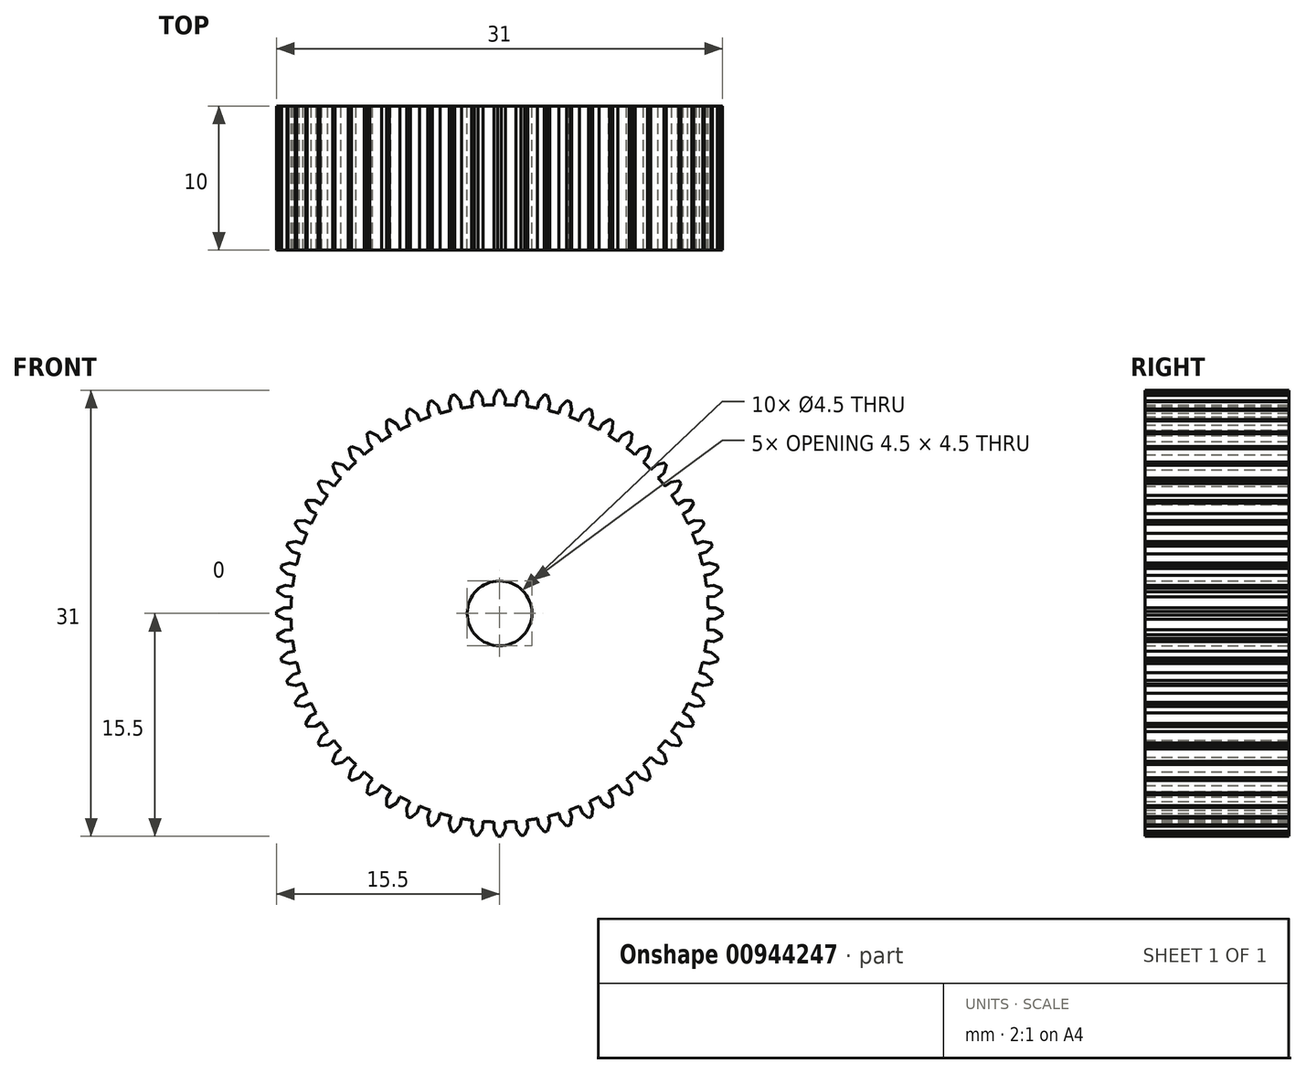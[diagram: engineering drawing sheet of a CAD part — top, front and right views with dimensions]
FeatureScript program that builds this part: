
annotation { "Feature Type Name" : "Feature", "Feature Type Description" : "" }
export const myFeature = defineFeature(function(context is Context, id is Id, definition is map)
    precondition{}
    {
        {
            var Q0;
            Q0=qCreatedBy(makeId("Front.planeOp"),FACE);
            var sketch = newSketch(context, id + "F0", { "sketchPlane" : qUnion([Q0])});
            skCircle(sketch, "E0", {"center": v(0, 0) * mm, "radius": 14.5 * mm});
            skCircle(sketch, "E1", {"center": v(0, 0) * mm, "radius": 15 * mm, "construction": true});
            skCircle(sketch, "E2", {"center": v(0, 0) * mm, "radius": 15.5 * mm, "construction": true});
            skLineSegment(sketch, "E3", {"start": v(0, 0) * mm, "end": v(0, 25.34) * mm, "construction": true});
            skLineSegment(sketch, "E4", {"start": v(0, 25.34) * mm, "end": v(0, 0) * mm, "construction": true});
            skLineSegment(sketch, "E5", {"start": v(-0.38, 14.5) * mm, "end": v(-0.4, 15) * mm});
            skLineSegment(sketch, "E6", {"start": v(0.38, 14.5) * mm, "end": v(0.4, 15) * mm});
            skLineSegment(sketch, "E7", {"start": v(-0.39, 15) * mm, "end": v(-0.12, 15.5) * mm});
            skLineSegment(sketch, "E8", {"start": v(0.39, 15) * mm, "end": v(0.12, 15.5) * mm});
            skArc(sketch, "E9", {"start": v(-0.12, 15.5) * mm, "mid": v(0, 15.5) * mm, "end": v(0.12, 15.5) * mm});
            skPoint(sketch, "E10.newPointB", {"position": v(-0.57, 21.86) * mm});
            skArc(sketch, "E10.filletArc", {"start": v(-0.39, 15) * mm, "mid": v(-0.4, 15) * mm, "end": v(-0.4, 14.98) * mm});
            skPoint(sketch, "E11.newPointA", {"position": v(0.57, 21.86) * mm});
            skArc(sketch, "E11.filletArc", {"start": v(0.4, 14.98) * mm, "mid": v(0.4, 15) * mm, "end": v(0.39, 15) * mm});
            skLineSegment(sketch, "E12.1.0", {"start": v(-1.14, 14.46) * mm, "end": v(-1.18, 14.95) * mm});
            skLineSegment(sketch, "E12.1.1", {"start": v(-1.9, 14.38) * mm, "end": v(-1.96, 14.87) * mm});
            skArc(sketch, "E12.1.2", {"start": v(-1.95, 14.88) * mm, "mid": v(-1.96, 14.87) * mm, "end": v(-1.96, 14.86) * mm});
            skLineSegment(sketch, "E12.1.3", {"start": v(-1.95, 14.88) * mm, "end": v(-1.74, 15.4) * mm});
            skArc(sketch, "E12.1.4", {"start": v(-1.18, 14.94) * mm, "mid": v(-1.18, 14.95) * mm, "end": v(-1.18, 14.96) * mm});
            skLineSegment(sketch, "E12.1.5", {"start": v(-1.18, 14.96) * mm, "end": v(-1.5, 15.43) * mm});
            skArc(sketch, "E12.1.6", {"start": v(-1.74, 15.4) * mm, "mid": v(-1.62, 15.42) * mm, "end": v(-1.5, 15.43) * mm});
            skLineSegment(sketch, "E12.2.0", {"start": v(-2.64, 14.26) * mm, "end": v(-2.73, 14.75) * mm});
            skLineSegment(sketch, "E12.2.1", {"start": v(-3.38, 14.1) * mm, "end": v(-3.5, 14.59) * mm});
            skArc(sketch, "E12.2.2", {"start": v(-3.5, 14.6) * mm, "mid": v(-3.5, 14.59) * mm, "end": v(-3.5, 14.57) * mm});
            skLineSegment(sketch, "E12.2.3", {"start": v(-3.5, 14.6) * mm, "end": v(-3.34, 15.14) * mm});
            skArc(sketch, "E12.2.4", {"start": v(-2.73, 14.74) * mm, "mid": v(-2.74, 14.75) * mm, "end": v(-2.74, 14.76) * mm});
            skLineSegment(sketch, "E12.2.5", {"start": v(-2.74, 14.76) * mm, "end": v(-3.1, 15.19) * mm});
            skArc(sketch, "E12.2.6", {"start": v(-3.34, 15.14) * mm, "mid": v(-3.22, 15.16) * mm, "end": v(-3.1, 15.19) * mm});
            skLineSegment(sketch, "E12.3.0", {"start": v(-4.12, 13.9) * mm, "end": v(-4.26, 14.38) * mm});
            skLineSegment(sketch, "E12.3.1", {"start": v(-4.84, 13.67) * mm, "end": v(-5, 14.14) * mm});
            skArc(sketch, "E12.3.2", {"start": v(-5, 14.15) * mm, "mid": v(-5, 14.14) * mm, "end": v(-5, 14.13) * mm});
            skLineSegment(sketch, "E12.3.3", {"start": v(-5, 14.15) * mm, "end": v(-4.9, 14.7) * mm});
            skArc(sketch, "E12.3.4", {"start": v(-4.26, 14.37) * mm, "mid": v(-4.26, 14.38) * mm, "end": v(-4.27, 14.4) * mm});
            skLineSegment(sketch, "E12.3.5", {"start": v(-4.27, 14.4) * mm, "end": v(-4.68, 14.78) * mm});
            skArc(sketch, "E12.3.6", {"start": v(-4.9, 14.7) * mm, "mid": v(-4.79, 14.74) * mm, "end": v(-4.68, 14.78) * mm});
            skLineSegment(sketch, "E12.4.0", {"start": v(-5.55, 13.4) * mm, "end": v(-5.74, 13.86) * mm});
            skLineSegment(sketch, "E12.4.1", {"start": v(-6.24, 13.09) * mm, "end": v(-6.46, 13.54) * mm});
            skArc(sketch, "E12.4.2", {"start": v(-6.46, 13.55) * mm, "mid": v(-6.46, 13.54) * mm, "end": v(-6.45, 13.53) * mm});
            skLineSegment(sketch, "E12.4.3", {"start": v(-6.46, 13.55) * mm, "end": v(-6.41, 14.11) * mm});
            skArc(sketch, "E12.4.4", {"start": v(-5.74, 13.85) * mm, "mid": v(-5.74, 13.86) * mm, "end": v(-5.75, 13.87) * mm});
            skLineSegment(sketch, "E12.4.5", {"start": v(-5.75, 13.87) * mm, "end": v(-6.2, 14.2) * mm});
            skArc(sketch, "E12.4.6", {"start": v(-6.41, 14.11) * mm, "mid": v(-6.3, 14.16) * mm, "end": v(-6.2, 14.2) * mm});
            skLineSegment(sketch, "E12.5.0", {"start": v(-6.92, 12.74) * mm, "end": v(-7.16, 13.18) * mm});
            skLineSegment(sketch, "E12.5.1", {"start": v(-7.58, 12.36) * mm, "end": v(-7.84, 12.79) * mm});
            skArc(sketch, "E12.5.2", {"start": v(-7.84, 12.8) * mm, "mid": v(-7.84, 12.8) * mm, "end": v(-7.83, 12.78) * mm});
            skLineSegment(sketch, "E12.5.3", {"start": v(-7.84, 12.8) * mm, "end": v(-7.85, 13.36) * mm});
            skArc(sketch, "E12.5.4", {"start": v(-7.15, 13.17) * mm, "mid": v(-7.16, 13.18) * mm, "end": v(-7.17, 13.19) * mm});
            skLineSegment(sketch, "E12.5.5", {"start": v(-7.17, 13.19) * mm, "end": v(-7.65, 13.48) * mm});
            skArc(sketch, "E12.5.6", {"start": v(-7.85, 13.36) * mm, "mid": v(-7.75, 13.42) * mm, "end": v(-7.65, 13.48) * mm});
            skLineSegment(sketch, "E12.6.0", {"start": v(-8.21, 11.95) * mm, "end": v(-8.5, 12.36) * mm});
            skLineSegment(sketch, "E12.6.1", {"start": v(-8.83, 11.5) * mm, "end": v(-9.13, 11.9) * mm});
            skArc(sketch, "E12.6.2", {"start": v(-9.13, 11.91) * mm, "mid": v(-9.13, 11.9) * mm, "end": v(-9.12, 11.89) * mm});
            skLineSegment(sketch, "E12.6.3", {"start": v(-9.13, 11.91) * mm, "end": v(-9.2, 12.47) * mm});
            skArc(sketch, "E12.6.4", {"start": v(-8.49, 12.35) * mm, "mid": v(-8.5, 12.36) * mm, "end": v(-8.5, 12.37) * mm});
            skLineSegment(sketch, "E12.6.5", {"start": v(-8.5, 12.37) * mm, "end": v(-9.01, 12.6) * mm});
            skArc(sketch, "E12.6.6", {"start": v(-9.2, 12.47) * mm, "mid": v(-9.11, 12.54) * mm, "end": v(-9.01, 12.6) * mm});
            skLineSegment(sketch, "E12.7.0", {"start": v(-9.42, 11.03) * mm, "end": v(-9.74, 11.4) * mm});
            skLineSegment(sketch, "E12.7.1", {"start": v(-9.98, 10.52) * mm, "end": v(-10.33, 10.88) * mm});
            skArc(sketch, "E12.7.2", {"start": v(-10.33, 10.9) * mm, "mid": v(-10.32, 10.88) * mm, "end": v(-10.32, 10.87) * mm});
            skLineSegment(sketch, "E12.7.3", {"start": v(-10.33, 10.9) * mm, "end": v(-10.46, 11.44) * mm});
            skArc(sketch, "E12.7.4", {"start": v(-9.73, 11.4) * mm, "mid": v(-9.74, 11.4) * mm, "end": v(-9.75, 11.41) * mm});
            skLineSegment(sketch, "E12.7.5", {"start": v(-9.75, 11.41) * mm, "end": v(-10.28, 11.6) * mm});
            skArc(sketch, "E12.7.6", {"start": v(-10.46, 11.44) * mm, "mid": v(-10.37, 11.52) * mm, "end": v(-10.28, 11.6) * mm});
            skLineSegment(sketch, "E12.8.0", {"start": v(-10.52, 9.98) * mm, "end": v(-10.88, 10.33) * mm});
            skLineSegment(sketch, "E12.8.1", {"start": v(-11.03, 9.42) * mm, "end": v(-11.4, 9.74) * mm});
            skArc(sketch, "E12.8.2", {"start": v(-11.41, 9.75) * mm, "mid": v(-11.4, 9.74) * mm, "end": v(-11.4, 9.73) * mm});
            skLineSegment(sketch, "E12.8.3", {"start": v(-11.41, 9.75) * mm, "end": v(-11.6, 10.28) * mm});
            skArc(sketch, "E12.8.4", {"start": v(-10.87, 10.32) * mm, "mid": v(-10.88, 10.32) * mm, "end": v(-10.9, 10.33) * mm});
            skLineSegment(sketch, "E12.8.5", {"start": v(-10.9, 10.33) * mm, "end": v(-11.44, 10.46) * mm});
            skArc(sketch, "E12.8.6", {"start": v(-11.6, 10.28) * mm, "mid": v(-11.52, 10.37) * mm, "end": v(-11.44, 10.46) * mm});
            skLineSegment(sketch, "E12.9.0", {"start": v(-11.5, 8.83) * mm, "end": v(-11.9, 9.13) * mm});
            skLineSegment(sketch, "E12.9.1", {"start": v(-11.95, 8.21) * mm, "end": v(-12.36, 8.5) * mm});
            skArc(sketch, "E12.9.2", {"start": v(-12.37, 8.5) * mm, "mid": v(-12.36, 8.5) * mm, "end": v(-12.35, 8.49) * mm});
            skLineSegment(sketch, "E12.9.3", {"start": v(-12.37, 8.5) * mm, "end": v(-12.6, 9.01) * mm});
            skArc(sketch, "E12.9.4", {"start": v(-11.89, 9.12) * mm, "mid": v(-11.9, 9.13) * mm, "end": v(-11.91, 9.13) * mm});
            skLineSegment(sketch, "E12.9.5", {"start": v(-11.91, 9.13) * mm, "end": v(-12.47, 9.2) * mm});
            skArc(sketch, "E12.9.6", {"start": v(-12.6, 9.01) * mm, "mid": v(-12.54, 9.11) * mm, "end": v(-12.47, 9.2) * mm});
            skLineSegment(sketch, "E12.10.0", {"start": v(-12.36, 7.58) * mm, "end": v(-12.79, 7.84) * mm});
            skLineSegment(sketch, "E12.10.1", {"start": v(-12.74, 6.92) * mm, "end": v(-13.18, 7.16) * mm});
            skArc(sketch, "E12.10.2", {"start": v(-13.19, 7.17) * mm, "mid": v(-13.18, 7.16) * mm, "end": v(-13.17, 7.15) * mm});
            skLineSegment(sketch, "E12.10.3", {"start": v(-13.19, 7.17) * mm, "end": v(-13.48, 7.65) * mm});
            skArc(sketch, "E12.10.4", {"start": v(-12.78, 7.83) * mm, "mid": v(-12.8, 7.84) * mm, "end": v(-12.8, 7.84) * mm});
            skLineSegment(sketch, "E12.10.5", {"start": v(-12.8, 7.84) * mm, "end": v(-13.36, 7.85) * mm});
            skArc(sketch, "E12.10.6", {"start": v(-13.48, 7.65) * mm, "mid": v(-13.42, 7.75) * mm, "end": v(-13.36, 7.85) * mm});
            skLineSegment(sketch, "E12.11.0", {"start": v(-13.09, 6.24) * mm, "end": v(-13.54, 6.46) * mm});
            skLineSegment(sketch, "E12.11.1", {"start": v(-13.4, 5.55) * mm, "end": v(-13.86, 5.74) * mm});
            skArc(sketch, "E12.11.2", {"start": v(-13.87, 5.75) * mm, "mid": v(-13.86, 5.74) * mm, "end": v(-13.85, 5.74) * mm});
            skLineSegment(sketch, "E12.11.3", {"start": v(-13.87, 5.75) * mm, "end": v(-14.2, 6.2) * mm});
            skArc(sketch, "E12.11.4", {"start": v(-13.53, 6.45) * mm, "mid": v(-13.54, 6.46) * mm, "end": v(-13.55, 6.46) * mm});
            skLineSegment(sketch, "E12.11.5", {"start": v(-13.55, 6.46) * mm, "end": v(-14.11, 6.41) * mm});
            skArc(sketch, "E12.11.6", {"start": v(-14.2, 6.2) * mm, "mid": v(-14.16, 6.3) * mm, "end": v(-14.11, 6.41) * mm});
            skLineSegment(sketch, "E12.12.0", {"start": v(-13.67, 4.84) * mm, "end": v(-14.14, 5) * mm});
            skLineSegment(sketch, "E12.12.1", {"start": v(-13.9, 4.12) * mm, "end": v(-14.38, 4.26) * mm});
            skArc(sketch, "E12.12.2", {"start": v(-14.4, 4.27) * mm, "mid": v(-14.38, 4.26) * mm, "end": v(-14.37, 4.26) * mm});
            skLineSegment(sketch, "E12.12.3", {"start": v(-14.4, 4.27) * mm, "end": v(-14.78, 4.68) * mm});
            skArc(sketch, "E12.12.4", {"start": v(-14.13, 5) * mm, "mid": v(-14.14, 5) * mm, "end": v(-14.15, 5) * mm});
            skLineSegment(sketch, "E12.12.5", {"start": v(-14.15, 5) * mm, "end": v(-14.7, 4.9) * mm});
            skArc(sketch, "E12.12.6", {"start": v(-14.78, 4.68) * mm, "mid": v(-14.74, 4.79) * mm, "end": v(-14.7, 4.9) * mm});
            skLineSegment(sketch, "E12.13.0", {"start": v(-14.1, 3.38) * mm, "end": v(-14.59, 3.5) * mm});
            skLineSegment(sketch, "E12.13.1", {"start": v(-14.26, 2.64) * mm, "end": v(-14.75, 2.73) * mm});
            skArc(sketch, "E12.13.2", {"start": v(-14.76, 2.74) * mm, "mid": v(-14.75, 2.74) * mm, "end": v(-14.74, 2.73) * mm});
            skLineSegment(sketch, "E12.13.3", {"start": v(-14.76, 2.74) * mm, "end": v(-15.19, 3.1) * mm});
            skArc(sketch, "E12.13.4", {"start": v(-14.57, 3.5) * mm, "mid": v(-14.59, 3.5) * mm, "end": v(-14.6, 3.5) * mm});
            skLineSegment(sketch, "E12.13.5", {"start": v(-14.6, 3.5) * mm, "end": v(-15.14, 3.34) * mm});
            skArc(sketch, "E12.13.6", {"start": v(-15.19, 3.1) * mm, "mid": v(-15.16, 3.22) * mm, "end": v(-15.14, 3.34) * mm});
            skLineSegment(sketch, "E12.14.0", {"start": v(-14.38, 1.9) * mm, "end": v(-14.87, 1.96) * mm});
            skLineSegment(sketch, "E12.14.1", {"start": v(-14.46, 1.14) * mm, "end": v(-14.95, 1.18) * mm});
            skArc(sketch, "E12.14.2", {"start": v(-14.96, 1.18) * mm, "mid": v(-14.95, 1.18) * mm, "end": v(-14.94, 1.18) * mm});
            skLineSegment(sketch, "E12.14.3", {"start": v(-14.96, 1.18) * mm, "end": v(-15.43, 1.5) * mm});
            skArc(sketch, "E12.14.4", {"start": v(-14.86, 1.96) * mm, "mid": v(-14.87, 1.96) * mm, "end": v(-14.88, 1.95) * mm});
            skLineSegment(sketch, "E12.14.5", {"start": v(-14.88, 1.95) * mm, "end": v(-15.4, 1.74) * mm});
            skArc(sketch, "E12.14.6", {"start": v(-15.43, 1.5) * mm, "mid": v(-15.42, 1.62) * mm, "end": v(-15.4, 1.74) * mm});
            skLineSegment(sketch, "E12.15.0", {"start": v(-14.5, 0.38) * mm, "end": v(-15, 0.4) * mm});
            skLineSegment(sketch, "E12.15.1", {"start": v(-14.5, -0.38) * mm, "end": v(-15, -0.4) * mm});
            skArc(sketch, "E12.15.2", {"start": v(-15, -0.39) * mm, "mid": v(-15, -0.4) * mm, "end": v(-14.98, -0.4) * mm});
            skLineSegment(sketch, "E12.15.3", {"start": v(-15, -0.39) * mm, "end": v(-15.5, -0.12) * mm});
            skArc(sketch, "E12.15.4", {"start": v(-14.98, 0.4) * mm, "mid": v(-15, 0.4) * mm, "end": v(-15, 0.39) * mm});
            skLineSegment(sketch, "E12.15.5", {"start": v(-15, 0.39) * mm, "end": v(-15.5, 0.12) * mm});
            skArc(sketch, "E12.15.6", {"start": v(-15.5, -0.12) * mm, "mid": v(-15.5, 0) * mm, "end": v(-15.5, 0.12) * mm});
            skLineSegment(sketch, "E12.16.0", {"start": v(-14.46, -1.14) * mm, "end": v(-14.95, -1.18) * mm});
            skLineSegment(sketch, "E12.16.1", {"start": v(-14.38, -1.9) * mm, "end": v(-14.87, -1.96) * mm});
            skArc(sketch, "E12.16.2", {"start": v(-14.88, -1.95) * mm, "mid": v(-14.87, -1.96) * mm, "end": v(-14.86, -1.96) * mm});
            skLineSegment(sketch, "E12.16.3", {"start": v(-14.88, -1.95) * mm, "end": v(-15.4, -1.74) * mm});
            skArc(sketch, "E12.16.4", {"start": v(-14.94, -1.18) * mm, "mid": v(-14.95, -1.18) * mm, "end": v(-14.96, -1.18) * mm});
            skLineSegment(sketch, "E12.16.5", {"start": v(-14.96, -1.18) * mm, "end": v(-15.43, -1.5) * mm});
            skArc(sketch, "E12.16.6", {"start": v(-15.4, -1.74) * mm, "mid": v(-15.42, -1.62) * mm, "end": v(-15.43, -1.5) * mm});
            skLineSegment(sketch, "E12.17.0", {"start": v(-14.26, -2.64) * mm, "end": v(-14.75, -2.73) * mm});
            skLineSegment(sketch, "E12.17.1", {"start": v(-14.1, -3.38) * mm, "end": v(-14.59, -3.5) * mm});
            skArc(sketch, "E12.17.2", {"start": v(-14.6, -3.5) * mm, "mid": v(-14.59, -3.5) * mm, "end": v(-14.57, -3.5) * mm});
            skLineSegment(sketch, "E12.17.3", {"start": v(-14.6, -3.5) * mm, "end": v(-15.14, -3.34) * mm});
            skArc(sketch, "E12.17.4", {"start": v(-14.74, -2.73) * mm, "mid": v(-14.75, -2.74) * mm, "end": v(-14.76, -2.74) * mm});
            skLineSegment(sketch, "E12.17.5", {"start": v(-14.76, -2.74) * mm, "end": v(-15.19, -3.1) * mm});
            skArc(sketch, "E12.17.6", {"start": v(-15.14, -3.34) * mm, "mid": v(-15.16, -3.22) * mm, "end": v(-15.19, -3.1) * mm});
            skLineSegment(sketch, "E12.18.0", {"start": v(-13.9, -4.12) * mm, "end": v(-14.38, -4.26) * mm});
            skLineSegment(sketch, "E12.18.1", {"start": v(-13.67, -4.84) * mm, "end": v(-14.14, -5) * mm});
            skArc(sketch, "E12.18.2", {"start": v(-14.15, -5) * mm, "mid": v(-14.14, -5) * mm, "end": v(-14.13, -5) * mm});
            skLineSegment(sketch, "E12.18.3", {"start": v(-14.15, -5) * mm, "end": v(-14.7, -4.9) * mm});
            skArc(sketch, "E12.18.4", {"start": v(-14.37, -4.26) * mm, "mid": v(-14.38, -4.26) * mm, "end": v(-14.4, -4.27) * mm});
            skLineSegment(sketch, "E12.18.5", {"start": v(-14.4, -4.27) * mm, "end": v(-14.78, -4.68) * mm});
            skArc(sketch, "E12.18.6", {"start": v(-14.7, -4.9) * mm, "mid": v(-14.74, -4.79) * mm, "end": v(-14.78, -4.68) * mm});
            skLineSegment(sketch, "E12.19.0", {"start": v(-13.4, -5.55) * mm, "end": v(-13.86, -5.74) * mm});
            skLineSegment(sketch, "E12.19.1", {"start": v(-13.09, -6.24) * mm, "end": v(-13.54, -6.46) * mm});
            skArc(sketch, "E12.19.2", {"start": v(-13.55, -6.46) * mm, "mid": v(-13.54, -6.46) * mm, "end": v(-13.53, -6.45) * mm});
            skLineSegment(sketch, "E12.19.3", {"start": v(-13.55, -6.46) * mm, "end": v(-14.11, -6.41) * mm});
            skArc(sketch, "E12.19.4", {"start": v(-13.85, -5.74) * mm, "mid": v(-13.86, -5.74) * mm, "end": v(-13.87, -5.75) * mm});
            skLineSegment(sketch, "E12.19.5", {"start": v(-13.87, -5.75) * mm, "end": v(-14.2, -6.2) * mm});
            skArc(sketch, "E12.19.6", {"start": v(-14.11, -6.41) * mm, "mid": v(-14.16, -6.3) * mm, "end": v(-14.2, -6.2) * mm});
            skLineSegment(sketch, "E12.20.0", {"start": v(-12.74, -6.92) * mm, "end": v(-13.18, -7.16) * mm});
            skLineSegment(sketch, "E12.20.1", {"start": v(-12.36, -7.58) * mm, "end": v(-12.79, -7.84) * mm});
            skArc(sketch, "E12.20.2", {"start": v(-12.8, -7.84) * mm, "mid": v(-12.8, -7.84) * mm, "end": v(-12.78, -7.83) * mm});
            skLineSegment(sketch, "E12.20.3", {"start": v(-12.8, -7.84) * mm, "end": v(-13.36, -7.85) * mm});
            skArc(sketch, "E12.20.4", {"start": v(-13.17, -7.15) * mm, "mid": v(-13.18, -7.16) * mm, "end": v(-13.19, -7.17) * mm});
            skLineSegment(sketch, "E12.20.5", {"start": v(-13.19, -7.17) * mm, "end": v(-13.48, -7.65) * mm});
            skArc(sketch, "E12.20.6", {"start": v(-13.36, -7.85) * mm, "mid": v(-13.42, -7.75) * mm, "end": v(-13.48, -7.65) * mm});
            skLineSegment(sketch, "E12.21.0", {"start": v(-11.95, -8.21) * mm, "end": v(-12.36, -8.5) * mm});
            skLineSegment(sketch, "E12.21.1", {"start": v(-11.5, -8.83) * mm, "end": v(-11.9, -9.13) * mm});
            skArc(sketch, "E12.21.2", {"start": v(-11.91, -9.13) * mm, "mid": v(-11.9, -9.13) * mm, "end": v(-11.89, -9.12) * mm});
            skLineSegment(sketch, "E12.21.3", {"start": v(-11.91, -9.13) * mm, "end": v(-12.47, -9.2) * mm});
            skArc(sketch, "E12.21.4", {"start": v(-12.35, -8.49) * mm, "mid": v(-12.36, -8.5) * mm, "end": v(-12.37, -8.5) * mm});
            skLineSegment(sketch, "E12.21.5", {"start": v(-12.37, -8.5) * mm, "end": v(-12.6, -9.01) * mm});
            skArc(sketch, "E12.21.6", {"start": v(-12.47, -9.2) * mm, "mid": v(-12.54, -9.11) * mm, "end": v(-12.6, -9.01) * mm});
            skLineSegment(sketch, "E12.22.0", {"start": v(-11.03, -9.42) * mm, "end": v(-11.4, -9.74) * mm});
            skLineSegment(sketch, "E12.22.1", {"start": v(-10.52, -9.98) * mm, "end": v(-10.88, -10.33) * mm});
            skArc(sketch, "E12.22.2", {"start": v(-10.9, -10.33) * mm, "mid": v(-10.88, -10.32) * mm, "end": v(-10.87, -10.32) * mm});
            skLineSegment(sketch, "E12.22.3", {"start": v(-10.9, -10.33) * mm, "end": v(-11.44, -10.46) * mm});
            skArc(sketch, "E12.22.4", {"start": v(-11.4, -9.73) * mm, "mid": v(-11.4, -9.74) * mm, "end": v(-11.41, -9.75) * mm});
            skLineSegment(sketch, "E12.22.5", {"start": v(-11.41, -9.75) * mm, "end": v(-11.6, -10.28) * mm});
            skArc(sketch, "E12.22.6", {"start": v(-11.44, -10.46) * mm, "mid": v(-11.52, -10.37) * mm, "end": v(-11.6, -10.28) * mm});
            skLineSegment(sketch, "E12.23.0", {"start": v(-9.98, -10.52) * mm, "end": v(-10.33, -10.88) * mm});
            skLineSegment(sketch, "E12.23.1", {"start": v(-9.42, -11.03) * mm, "end": v(-9.74, -11.4) * mm});
            skArc(sketch, "E12.23.2", {"start": v(-9.75, -11.41) * mm, "mid": v(-9.74, -11.4) * mm, "end": v(-9.73, -11.4) * mm});
            skLineSegment(sketch, "E12.23.3", {"start": v(-9.75, -11.41) * mm, "end": v(-10.28, -11.6) * mm});
            skArc(sketch, "E12.23.4", {"start": v(-10.32, -10.87) * mm, "mid": v(-10.32, -10.88) * mm, "end": v(-10.33, -10.9) * mm});
            skLineSegment(sketch, "E12.23.5", {"start": v(-10.33, -10.9) * mm, "end": v(-10.46, -11.44) * mm});
            skArc(sketch, "E12.23.6", {"start": v(-10.28, -11.6) * mm, "mid": v(-10.37, -11.52) * mm, "end": v(-10.46, -11.44) * mm});
            skLineSegment(sketch, "E12.24.0", {"start": v(-8.83, -11.5) * mm, "end": v(-9.13, -11.9) * mm});
            skLineSegment(sketch, "E12.24.1", {"start": v(-8.21, -11.95) * mm, "end": v(-8.5, -12.36) * mm});
            skArc(sketch, "E12.24.2", {"start": v(-8.5, -12.37) * mm, "mid": v(-8.5, -12.36) * mm, "end": v(-8.49, -12.35) * mm});
            skLineSegment(sketch, "E12.24.3", {"start": v(-8.5, -12.37) * mm, "end": v(-9.01, -12.6) * mm});
            skArc(sketch, "E12.24.4", {"start": v(-9.12, -11.89) * mm, "mid": v(-9.13, -11.9) * mm, "end": v(-9.13, -11.91) * mm});
            skLineSegment(sketch, "E12.24.5", {"start": v(-9.13, -11.91) * mm, "end": v(-9.2, -12.47) * mm});
            skArc(sketch, "E12.24.6", {"start": v(-9.01, -12.6) * mm, "mid": v(-9.11, -12.54) * mm, "end": v(-9.2, -12.47) * mm});
            skLineSegment(sketch, "E12.25.0", {"start": v(-7.58, -12.36) * mm, "end": v(-7.84, -12.79) * mm});
            skLineSegment(sketch, "E12.25.1", {"start": v(-6.92, -12.74) * mm, "end": v(-7.16, -13.18) * mm});
            skArc(sketch, "E12.25.2", {"start": v(-7.17, -13.19) * mm, "mid": v(-7.16, -13.18) * mm, "end": v(-7.15, -13.17) * mm});
            skLineSegment(sketch, "E12.25.3", {"start": v(-7.17, -13.19) * mm, "end": v(-7.65, -13.48) * mm});
            skArc(sketch, "E12.25.4", {"start": v(-7.83, -12.78) * mm, "mid": v(-7.84, -12.8) * mm, "end": v(-7.84, -12.8) * mm});
            skLineSegment(sketch, "E12.25.5", {"start": v(-7.84, -12.8) * mm, "end": v(-7.85, -13.36) * mm});
            skArc(sketch, "E12.25.6", {"start": v(-7.65, -13.48) * mm, "mid": v(-7.75, -13.42) * mm, "end": v(-7.85, -13.36) * mm});
            skLineSegment(sketch, "E12.26.0", {"start": v(-6.24, -13.09) * mm, "end": v(-6.46, -13.54) * mm});
            skLineSegment(sketch, "E12.26.1", {"start": v(-5.55, -13.4) * mm, "end": v(-5.74, -13.86) * mm});
            skArc(sketch, "E12.26.2", {"start": v(-5.75, -13.87) * mm, "mid": v(-5.74, -13.86) * mm, "end": v(-5.74, -13.85) * mm});
            skLineSegment(sketch, "E12.26.3", {"start": v(-5.75, -13.87) * mm, "end": v(-6.2, -14.2) * mm});
            skArc(sketch, "E12.26.4", {"start": v(-6.45, -13.53) * mm, "mid": v(-6.46, -13.54) * mm, "end": v(-6.46, -13.55) * mm});
            skLineSegment(sketch, "E12.26.5", {"start": v(-6.46, -13.55) * mm, "end": v(-6.41, -14.11) * mm});
            skArc(sketch, "E12.26.6", {"start": v(-6.2, -14.2) * mm, "mid": v(-6.3, -14.16) * mm, "end": v(-6.41, -14.11) * mm});
            skLineSegment(sketch, "E12.27.0", {"start": v(-4.84, -13.67) * mm, "end": v(-5, -14.14) * mm});
            skLineSegment(sketch, "E12.27.1", {"start": v(-4.12, -13.9) * mm, "end": v(-4.26, -14.38) * mm});
            skArc(sketch, "E12.27.2", {"start": v(-4.27, -14.4) * mm, "mid": v(-4.26, -14.38) * mm, "end": v(-4.26, -14.37) * mm});
            skLineSegment(sketch, "E12.27.3", {"start": v(-4.27, -14.4) * mm, "end": v(-4.68, -14.78) * mm});
            skArc(sketch, "E12.27.4", {"start": v(-5, -14.13) * mm, "mid": v(-5, -14.14) * mm, "end": v(-5, -14.15) * mm});
            skLineSegment(sketch, "E12.27.5", {"start": v(-5, -14.15) * mm, "end": v(-4.9, -14.7) * mm});
            skArc(sketch, "E12.27.6", {"start": v(-4.68, -14.78) * mm, "mid": v(-4.79, -14.74) * mm, "end": v(-4.9, -14.7) * mm});
            skLineSegment(sketch, "E12.28.0", {"start": v(-3.38, -14.1) * mm, "end": v(-3.5, -14.59) * mm});
            skLineSegment(sketch, "E12.28.1", {"start": v(-2.64, -14.26) * mm, "end": v(-2.73, -14.75) * mm});
            skArc(sketch, "E12.28.2", {"start": v(-2.74, -14.76) * mm, "mid": v(-2.74, -14.75) * mm, "end": v(-2.73, -14.74) * mm});
            skLineSegment(sketch, "E12.28.3", {"start": v(-2.74, -14.76) * mm, "end": v(-3.1, -15.19) * mm});
            skArc(sketch, "E12.28.4", {"start": v(-3.5, -14.57) * mm, "mid": v(-3.5, -14.59) * mm, "end": v(-3.5, -14.6) * mm});
            skLineSegment(sketch, "E12.28.5", {"start": v(-3.5, -14.6) * mm, "end": v(-3.34, -15.14) * mm});
            skArc(sketch, "E12.28.6", {"start": v(-3.1, -15.19) * mm, "mid": v(-3.22, -15.16) * mm, "end": v(-3.34, -15.14) * mm});
            skLineSegment(sketch, "E12.29.0", {"start": v(-1.9, -14.38) * mm, "end": v(-1.96, -14.87) * mm});
            skLineSegment(sketch, "E12.29.1", {"start": v(-1.14, -14.46) * mm, "end": v(-1.18, -14.95) * mm});
            skArc(sketch, "E12.29.2", {"start": v(-1.18, -14.96) * mm, "mid": v(-1.18, -14.95) * mm, "end": v(-1.18, -14.94) * mm});
            skLineSegment(sketch, "E12.29.3", {"start": v(-1.18, -14.96) * mm, "end": v(-1.5, -15.43) * mm});
            skArc(sketch, "E12.29.4", {"start": v(-1.96, -14.86) * mm, "mid": v(-1.96, -14.87) * mm, "end": v(-1.95, -14.88) * mm});
            skLineSegment(sketch, "E12.29.5", {"start": v(-1.95, -14.88) * mm, "end": v(-1.74, -15.4) * mm});
            skArc(sketch, "E12.29.6", {"start": v(-1.5, -15.43) * mm, "mid": v(-1.62, -15.42) * mm, "end": v(-1.74, -15.4) * mm});
            skLineSegment(sketch, "E12.30.0", {"start": v(-0.38, -14.5) * mm, "end": v(-0.4, -15) * mm});
            skLineSegment(sketch, "E12.30.1", {"start": v(0.38, -14.5) * mm, "end": v(0.4, -15) * mm});
            skArc(sketch, "E12.30.2", {"start": v(0.39, -15) * mm, "mid": v(0.4, -15) * mm, "end": v(0.4, -14.98) * mm});
            skLineSegment(sketch, "E12.30.3", {"start": v(0.39, -15) * mm, "end": v(0.12, -15.5) * mm});
            skArc(sketch, "E12.30.4", {"start": v(-0.4, -14.98) * mm, "mid": v(-0.4, -15) * mm, "end": v(-0.39, -15) * mm});
            skLineSegment(sketch, "E12.30.5", {"start": v(-0.39, -15) * mm, "end": v(-0.12, -15.5) * mm});
            skArc(sketch, "E12.30.6", {"start": v(0.12, -15.5) * mm, "mid": v(0, -15.5) * mm, "end": v(-0.12, -15.5) * mm});
            skLineSegment(sketch, "E12.31.0", {"start": v(1.14, -14.46) * mm, "end": v(1.18, -14.95) * mm});
            skLineSegment(sketch, "E12.31.1", {"start": v(1.9, -14.38) * mm, "end": v(1.96, -14.87) * mm});
            skArc(sketch, "E12.31.2", {"start": v(1.95, -14.88) * mm, "mid": v(1.96, -14.87) * mm, "end": v(1.96, -14.86) * mm});
            skLineSegment(sketch, "E12.31.3", {"start": v(1.95, -14.88) * mm, "end": v(1.74, -15.4) * mm});
            skArc(sketch, "E12.31.4", {"start": v(1.18, -14.94) * mm, "mid": v(1.18, -14.95) * mm, "end": v(1.18, -14.96) * mm});
            skLineSegment(sketch, "E12.31.5", {"start": v(1.18, -14.96) * mm, "end": v(1.5, -15.43) * mm});
            skArc(sketch, "E12.31.6", {"start": v(1.74, -15.4) * mm, "mid": v(1.62, -15.42) * mm, "end": v(1.5, -15.43) * mm});
            skLineSegment(sketch, "E12.32.0", {"start": v(2.64, -14.26) * mm, "end": v(2.73, -14.75) * mm});
            skLineSegment(sketch, "E12.32.1", {"start": v(3.38, -14.1) * mm, "end": v(3.5, -14.59) * mm});
            skArc(sketch, "E12.32.2", {"start": v(3.5, -14.6) * mm, "mid": v(3.5, -14.59) * mm, "end": v(3.5, -14.57) * mm});
            skLineSegment(sketch, "E12.32.3", {"start": v(3.5, -14.6) * mm, "end": v(3.34, -15.14) * mm});
            skArc(sketch, "E12.32.4", {"start": v(2.73, -14.74) * mm, "mid": v(2.74, -14.75) * mm, "end": v(2.74, -14.76) * mm});
            skLineSegment(sketch, "E12.32.5", {"start": v(2.74, -14.76) * mm, "end": v(3.1, -15.19) * mm});
            skArc(sketch, "E12.32.6", {"start": v(3.34, -15.14) * mm, "mid": v(3.22, -15.16) * mm, "end": v(3.1, -15.19) * mm});
            skLineSegment(sketch, "E12.33.0", {"start": v(4.12, -13.9) * mm, "end": v(4.26, -14.38) * mm});
            skLineSegment(sketch, "E12.33.1", {"start": v(4.84, -13.67) * mm, "end": v(5, -14.14) * mm});
            skArc(sketch, "E12.33.2", {"start": v(5, -14.15) * mm, "mid": v(5, -14.14) * mm, "end": v(5, -14.13) * mm});
            skLineSegment(sketch, "E12.33.3", {"start": v(5, -14.15) * mm, "end": v(4.9, -14.7) * mm});
            skArc(sketch, "E12.33.4", {"start": v(4.26, -14.37) * mm, "mid": v(4.26, -14.38) * mm, "end": v(4.27, -14.4) * mm});
            skLineSegment(sketch, "E12.33.5", {"start": v(4.27, -14.4) * mm, "end": v(4.68, -14.78) * mm});
            skArc(sketch, "E12.33.6", {"start": v(4.9, -14.7) * mm, "mid": v(4.79, -14.74) * mm, "end": v(4.68, -14.78) * mm});
            skLineSegment(sketch, "E12.34.0", {"start": v(5.55, -13.4) * mm, "end": v(5.74, -13.86) * mm});
            skLineSegment(sketch, "E12.34.1", {"start": v(6.24, -13.09) * mm, "end": v(6.46, -13.54) * mm});
            skArc(sketch, "E12.34.2", {"start": v(6.46, -13.55) * mm, "mid": v(6.46, -13.54) * mm, "end": v(6.45, -13.53) * mm});
            skLineSegment(sketch, "E12.34.3", {"start": v(6.46, -13.55) * mm, "end": v(6.41, -14.11) * mm});
            skArc(sketch, "E12.34.4", {"start": v(5.74, -13.85) * mm, "mid": v(5.74, -13.86) * mm, "end": v(5.75, -13.87) * mm});
            skLineSegment(sketch, "E12.34.5", {"start": v(5.75, -13.87) * mm, "end": v(6.2, -14.2) * mm});
            skArc(sketch, "E12.34.6", {"start": v(6.41, -14.11) * mm, "mid": v(6.3, -14.16) * mm, "end": v(6.2, -14.2) * mm});
            skLineSegment(sketch, "E12.35.0", {"start": v(6.92, -12.74) * mm, "end": v(7.16, -13.18) * mm});
            skLineSegment(sketch, "E12.35.1", {"start": v(7.58, -12.36) * mm, "end": v(7.84, -12.79) * mm});
            skArc(sketch, "E12.35.2", {"start": v(7.84, -12.8) * mm, "mid": v(7.84, -12.8) * mm, "end": v(7.83, -12.78) * mm});
            skLineSegment(sketch, "E12.35.3", {"start": v(7.84, -12.8) * mm, "end": v(7.85, -13.36) * mm});
            skArc(sketch, "E12.35.4", {"start": v(7.15, -13.17) * mm, "mid": v(7.16, -13.18) * mm, "end": v(7.17, -13.19) * mm});
            skLineSegment(sketch, "E12.35.5", {"start": v(7.17, -13.19) * mm, "end": v(7.65, -13.48) * mm});
            skArc(sketch, "E12.35.6", {"start": v(7.85, -13.36) * mm, "mid": v(7.75, -13.42) * mm, "end": v(7.65, -13.48) * mm});
            skLineSegment(sketch, "E12.36.0", {"start": v(8.21, -11.95) * mm, "end": v(8.5, -12.36) * mm});
            skLineSegment(sketch, "E12.36.1", {"start": v(8.83, -11.5) * mm, "end": v(9.13, -11.9) * mm});
            skArc(sketch, "E12.36.2", {"start": v(9.13, -11.91) * mm, "mid": v(9.13, -11.9) * mm, "end": v(9.12, -11.89) * mm});
            skLineSegment(sketch, "E12.36.3", {"start": v(9.13, -11.91) * mm, "end": v(9.2, -12.47) * mm});
            skArc(sketch, "E12.36.4", {"start": v(8.49, -12.35) * mm, "mid": v(8.5, -12.36) * mm, "end": v(8.5, -12.37) * mm});
            skLineSegment(sketch, "E12.36.5", {"start": v(8.5, -12.37) * mm, "end": v(9.01, -12.6) * mm});
            skArc(sketch, "E12.36.6", {"start": v(9.2, -12.47) * mm, "mid": v(9.11, -12.54) * mm, "end": v(9.01, -12.6) * mm});
            skLineSegment(sketch, "E12.37.0", {"start": v(9.42, -11.03) * mm, "end": v(9.74, -11.4) * mm});
            skLineSegment(sketch, "E12.37.1", {"start": v(9.98, -10.52) * mm, "end": v(10.33, -10.88) * mm});
            skArc(sketch, "E12.37.2", {"start": v(10.33, -10.9) * mm, "mid": v(10.32, -10.88) * mm, "end": v(10.32, -10.87) * mm});
            skLineSegment(sketch, "E12.37.3", {"start": v(10.33, -10.9) * mm, "end": v(10.46, -11.44) * mm});
            skArc(sketch, "E12.37.4", {"start": v(9.73, -11.4) * mm, "mid": v(9.74, -11.4) * mm, "end": v(9.75, -11.41) * mm});
            skLineSegment(sketch, "E12.37.5", {"start": v(9.75, -11.41) * mm, "end": v(10.28, -11.6) * mm});
            skArc(sketch, "E12.37.6", {"start": v(10.46, -11.44) * mm, "mid": v(10.37, -11.52) * mm, "end": v(10.28, -11.6) * mm});
            skLineSegment(sketch, "E12.38.0", {"start": v(10.52, -9.98) * mm, "end": v(10.88, -10.33) * mm});
            skLineSegment(sketch, "E12.38.1", {"start": v(11.03, -9.42) * mm, "end": v(11.4, -9.74) * mm});
            skArc(sketch, "E12.38.2", {"start": v(11.41, -9.75) * mm, "mid": v(11.4, -9.74) * mm, "end": v(11.4, -9.73) * mm});
            skLineSegment(sketch, "E12.38.3", {"start": v(11.41, -9.75) * mm, "end": v(11.6, -10.28) * mm});
            skArc(sketch, "E12.38.4", {"start": v(10.87, -10.32) * mm, "mid": v(10.88, -10.32) * mm, "end": v(10.9, -10.33) * mm});
            skLineSegment(sketch, "E12.38.5", {"start": v(10.9, -10.33) * mm, "end": v(11.44, -10.46) * mm});
            skArc(sketch, "E12.38.6", {"start": v(11.6, -10.28) * mm, "mid": v(11.52, -10.37) * mm, "end": v(11.44, -10.46) * mm});
            skLineSegment(sketch, "E12.39.0", {"start": v(11.5, -8.83) * mm, "end": v(11.9, -9.13) * mm});
            skLineSegment(sketch, "E12.39.1", {"start": v(11.95, -8.21) * mm, "end": v(12.36, -8.5) * mm});
            skArc(sketch, "E12.39.2", {"start": v(12.37, -8.5) * mm, "mid": v(12.36, -8.5) * mm, "end": v(12.35, -8.49) * mm});
            skLineSegment(sketch, "E12.39.3", {"start": v(12.37, -8.5) * mm, "end": v(12.6, -9.01) * mm});
            skArc(sketch, "E12.39.4", {"start": v(11.89, -9.12) * mm, "mid": v(11.9, -9.13) * mm, "end": v(11.91, -9.13) * mm});
            skLineSegment(sketch, "E12.39.5", {"start": v(11.91, -9.13) * mm, "end": v(12.47, -9.2) * mm});
            skArc(sketch, "E12.39.6", {"start": v(12.6, -9.01) * mm, "mid": v(12.54, -9.11) * mm, "end": v(12.47, -9.2) * mm});
            skLineSegment(sketch, "E12.40.0", {"start": v(12.36, -7.58) * mm, "end": v(12.79, -7.84) * mm});
            skLineSegment(sketch, "E12.40.1", {"start": v(12.74, -6.92) * mm, "end": v(13.18, -7.16) * mm});
            skArc(sketch, "E12.40.2", {"start": v(13.19, -7.17) * mm, "mid": v(13.18, -7.16) * mm, "end": v(13.17, -7.15) * mm});
            skLineSegment(sketch, "E12.40.3", {"start": v(13.19, -7.17) * mm, "end": v(13.48, -7.65) * mm});
            skArc(sketch, "E12.40.4", {"start": v(12.78, -7.83) * mm, "mid": v(12.8, -7.84) * mm, "end": v(12.8, -7.84) * mm});
            skLineSegment(sketch, "E12.40.5", {"start": v(12.8, -7.84) * mm, "end": v(13.36, -7.85) * mm});
            skArc(sketch, "E12.40.6", {"start": v(13.48, -7.65) * mm, "mid": v(13.42, -7.75) * mm, "end": v(13.36, -7.85) * mm});
            skLineSegment(sketch, "E12.41.0", {"start": v(13.09, -6.24) * mm, "end": v(13.54, -6.46) * mm});
            skLineSegment(sketch, "E12.41.1", {"start": v(13.4, -5.55) * mm, "end": v(13.86, -5.74) * mm});
            skArc(sketch, "E12.41.2", {"start": v(13.87, -5.75) * mm, "mid": v(13.86, -5.74) * mm, "end": v(13.85, -5.74) * mm});
            skLineSegment(sketch, "E12.41.3", {"start": v(13.87, -5.75) * mm, "end": v(14.2, -6.2) * mm});
            skArc(sketch, "E12.41.4", {"start": v(13.53, -6.45) * mm, "mid": v(13.54, -6.46) * mm, "end": v(13.55, -6.46) * mm});
            skLineSegment(sketch, "E12.41.5", {"start": v(13.55, -6.46) * mm, "end": v(14.11, -6.41) * mm});
            skArc(sketch, "E12.41.6", {"start": v(14.2, -6.2) * mm, "mid": v(14.16, -6.3) * mm, "end": v(14.11, -6.41) * mm});
            skLineSegment(sketch, "E12.42.0", {"start": v(13.67, -4.84) * mm, "end": v(14.14, -5) * mm});
            skLineSegment(sketch, "E12.42.1", {"start": v(13.9, -4.12) * mm, "end": v(14.38, -4.26) * mm});
            skArc(sketch, "E12.42.2", {"start": v(14.4, -4.27) * mm, "mid": v(14.38, -4.26) * mm, "end": v(14.37, -4.26) * mm});
            skLineSegment(sketch, "E12.42.3", {"start": v(14.4, -4.27) * mm, "end": v(14.78, -4.68) * mm});
            skArc(sketch, "E12.42.4", {"start": v(14.13, -5) * mm, "mid": v(14.14, -5) * mm, "end": v(14.15, -5) * mm});
            skLineSegment(sketch, "E12.42.5", {"start": v(14.15, -5) * mm, "end": v(14.7, -4.9) * mm});
            skArc(sketch, "E12.42.6", {"start": v(14.78, -4.68) * mm, "mid": v(14.74, -4.79) * mm, "end": v(14.7, -4.9) * mm});
            skLineSegment(sketch, "E12.43.0", {"start": v(14.1, -3.38) * mm, "end": v(14.59, -3.5) * mm});
            skLineSegment(sketch, "E12.43.1", {"start": v(14.26, -2.64) * mm, "end": v(14.75, -2.73) * mm});
            skArc(sketch, "E12.43.2", {"start": v(14.76, -2.74) * mm, "mid": v(14.75, -2.74) * mm, "end": v(14.74, -2.73) * mm});
            skLineSegment(sketch, "E12.43.3", {"start": v(14.76, -2.74) * mm, "end": v(15.19, -3.1) * mm});
            skArc(sketch, "E12.43.4", {"start": v(14.57, -3.5) * mm, "mid": v(14.59, -3.5) * mm, "end": v(14.6, -3.5) * mm});
            skLineSegment(sketch, "E12.43.5", {"start": v(14.6, -3.5) * mm, "end": v(15.14, -3.34) * mm});
            skArc(sketch, "E12.43.6", {"start": v(15.19, -3.1) * mm, "mid": v(15.16, -3.22) * mm, "end": v(15.14, -3.34) * mm});
            skLineSegment(sketch, "E12.44.0", {"start": v(14.38, -1.9) * mm, "end": v(14.87, -1.96) * mm});
            skLineSegment(sketch, "E12.44.1", {"start": v(14.46, -1.14) * mm, "end": v(14.95, -1.18) * mm});
            skArc(sketch, "E12.44.2", {"start": v(14.96, -1.18) * mm, "mid": v(14.95, -1.18) * mm, "end": v(14.94, -1.18) * mm});
            skLineSegment(sketch, "E12.44.3", {"start": v(14.96, -1.18) * mm, "end": v(15.43, -1.5) * mm});
            skArc(sketch, "E12.44.4", {"start": v(14.86, -1.96) * mm, "mid": v(14.87, -1.96) * mm, "end": v(14.88, -1.95) * mm});
            skLineSegment(sketch, "E12.44.5", {"start": v(14.88, -1.95) * mm, "end": v(15.4, -1.74) * mm});
            skArc(sketch, "E12.44.6", {"start": v(15.43, -1.5) * mm, "mid": v(15.42, -1.62) * mm, "end": v(15.4, -1.74) * mm});
            skLineSegment(sketch, "E12.45.0", {"start": v(14.5, -0.38) * mm, "end": v(15, -0.4) * mm});
            skLineSegment(sketch, "E12.45.1", {"start": v(14.5, 0.38) * mm, "end": v(15, 0.4) * mm});
            skArc(sketch, "E12.45.2", {"start": v(15, 0.39) * mm, "mid": v(15, 0.4) * mm, "end": v(14.98, 0.4) * mm});
            skLineSegment(sketch, "E12.45.3", {"start": v(15, 0.39) * mm, "end": v(15.5, 0.12) * mm});
            skArc(sketch, "E12.45.4", {"start": v(14.98, -0.4) * mm, "mid": v(15, -0.4) * mm, "end": v(15, -0.39) * mm});
            skLineSegment(sketch, "E12.45.5", {"start": v(15, -0.39) * mm, "end": v(15.5, -0.12) * mm});
            skArc(sketch, "E12.45.6", {"start": v(15.5, 0.12) * mm, "mid": v(15.5, 0) * mm, "end": v(15.5, -0.12) * mm});
            skLineSegment(sketch, "E12.46.0", {"start": v(14.46, 1.14) * mm, "end": v(14.95, 1.18) * mm});
            skLineSegment(sketch, "E12.46.1", {"start": v(14.38, 1.9) * mm, "end": v(14.87, 1.96) * mm});
            skArc(sketch, "E12.46.2", {"start": v(14.88, 1.95) * mm, "mid": v(14.87, 1.96) * mm, "end": v(14.86, 1.96) * mm});
            skLineSegment(sketch, "E12.46.3", {"start": v(14.88, 1.95) * mm, "end": v(15.4, 1.74) * mm});
            skArc(sketch, "E12.46.4", {"start": v(14.94, 1.18) * mm, "mid": v(14.95, 1.18) * mm, "end": v(14.96, 1.18) * mm});
            skLineSegment(sketch, "E12.46.5", {"start": v(14.96, 1.18) * mm, "end": v(15.43, 1.5) * mm});
            skArc(sketch, "E12.46.6", {"start": v(15.4, 1.74) * mm, "mid": v(15.42, 1.62) * mm, "end": v(15.43, 1.5) * mm});
            skLineSegment(sketch, "E12.47.0", {"start": v(14.26, 2.64) * mm, "end": v(14.75, 2.73) * mm});
            skLineSegment(sketch, "E12.47.1", {"start": v(14.1, 3.38) * mm, "end": v(14.59, 3.5) * mm});
            skArc(sketch, "E12.47.2", {"start": v(14.6, 3.5) * mm, "mid": v(14.59, 3.5) * mm, "end": v(14.57, 3.5) * mm});
            skLineSegment(sketch, "E12.47.3", {"start": v(14.6, 3.5) * mm, "end": v(15.14, 3.34) * mm});
            skArc(sketch, "E12.47.4", {"start": v(14.74, 2.73) * mm, "mid": v(14.75, 2.74) * mm, "end": v(14.76, 2.74) * mm});
            skLineSegment(sketch, "E12.47.5", {"start": v(14.76, 2.74) * mm, "end": v(15.19, 3.1) * mm});
            skArc(sketch, "E12.47.6", {"start": v(15.14, 3.34) * mm, "mid": v(15.16, 3.22) * mm, "end": v(15.19, 3.1) * mm});
            skLineSegment(sketch, "E12.48.0", {"start": v(13.9, 4.12) * mm, "end": v(14.38, 4.26) * mm});
            skLineSegment(sketch, "E12.48.1", {"start": v(13.67, 4.84) * mm, "end": v(14.14, 5) * mm});
            skArc(sketch, "E12.48.2", {"start": v(14.15, 5) * mm, "mid": v(14.14, 5) * mm, "end": v(14.13, 5) * mm});
            skLineSegment(sketch, "E12.48.3", {"start": v(14.15, 5) * mm, "end": v(14.7, 4.9) * mm});
            skArc(sketch, "E12.48.4", {"start": v(14.37, 4.26) * mm, "mid": v(14.38, 4.26) * mm, "end": v(14.4, 4.27) * mm});
            skLineSegment(sketch, "E12.48.5", {"start": v(14.4, 4.27) * mm, "end": v(14.78, 4.68) * mm});
            skArc(sketch, "E12.48.6", {"start": v(14.7, 4.9) * mm, "mid": v(14.74, 4.79) * mm, "end": v(14.78, 4.68) * mm});
            skLineSegment(sketch, "E12.49.0", {"start": v(13.4, 5.55) * mm, "end": v(13.86, 5.74) * mm});
            skLineSegment(sketch, "E12.49.1", {"start": v(13.09, 6.24) * mm, "end": v(13.54, 6.46) * mm});
            skArc(sketch, "E12.49.2", {"start": v(13.55, 6.46) * mm, "mid": v(13.54, 6.46) * mm, "end": v(13.53, 6.45) * mm});
            skLineSegment(sketch, "E12.49.3", {"start": v(13.55, 6.46) * mm, "end": v(14.11, 6.41) * mm});
            skArc(sketch, "E12.49.4", {"start": v(13.85, 5.74) * mm, "mid": v(13.86, 5.74) * mm, "end": v(13.87, 5.75) * mm});
            skLineSegment(sketch, "E12.49.5", {"start": v(13.87, 5.75) * mm, "end": v(14.2, 6.2) * mm});
            skArc(sketch, "E12.49.6", {"start": v(14.11, 6.41) * mm, "mid": v(14.16, 6.3) * mm, "end": v(14.2, 6.2) * mm});
            skLineSegment(sketch, "E12.50.0", {"start": v(12.74, 6.92) * mm, "end": v(13.18, 7.16) * mm});
            skLineSegment(sketch, "E12.50.1", {"start": v(12.36, 7.58) * mm, "end": v(12.79, 7.84) * mm});
            skArc(sketch, "E12.50.2", {"start": v(12.8, 7.84) * mm, "mid": v(12.8, 7.84) * mm, "end": v(12.78, 7.83) * mm});
            skLineSegment(sketch, "E12.50.3", {"start": v(12.8, 7.84) * mm, "end": v(13.36, 7.85) * mm});
            skArc(sketch, "E12.50.4", {"start": v(13.17, 7.15) * mm, "mid": v(13.18, 7.16) * mm, "end": v(13.19, 7.17) * mm});
            skLineSegment(sketch, "E12.50.5", {"start": v(13.19, 7.17) * mm, "end": v(13.48, 7.65) * mm});
            skArc(sketch, "E12.50.6", {"start": v(13.36, 7.85) * mm, "mid": v(13.42, 7.75) * mm, "end": v(13.48, 7.65) * mm});
            skLineSegment(sketch, "E12.51.0", {"start": v(11.95, 8.21) * mm, "end": v(12.36, 8.5) * mm});
            skLineSegment(sketch, "E12.51.1", {"start": v(11.5, 8.83) * mm, "end": v(11.9, 9.13) * mm});
            skArc(sketch, "E12.51.2", {"start": v(11.91, 9.13) * mm, "mid": v(11.9, 9.13) * mm, "end": v(11.89, 9.12) * mm});
            skLineSegment(sketch, "E12.51.3", {"start": v(11.91, 9.13) * mm, "end": v(12.47, 9.2) * mm});
            skArc(sketch, "E12.51.4", {"start": v(12.35, 8.49) * mm, "mid": v(12.36, 8.5) * mm, "end": v(12.37, 8.5) * mm});
            skLineSegment(sketch, "E12.51.5", {"start": v(12.37, 8.5) * mm, "end": v(12.6, 9.01) * mm});
            skArc(sketch, "E12.51.6", {"start": v(12.47, 9.2) * mm, "mid": v(12.54, 9.11) * mm, "end": v(12.6, 9.01) * mm});
            skLineSegment(sketch, "E12.52.0", {"start": v(11.03, 9.42) * mm, "end": v(11.4, 9.74) * mm});
            skLineSegment(sketch, "E12.52.1", {"start": v(10.52, 9.98) * mm, "end": v(10.88, 10.33) * mm});
            skArc(sketch, "E12.52.2", {"start": v(10.9, 10.33) * mm, "mid": v(10.88, 10.32) * mm, "end": v(10.87, 10.32) * mm});
            skLineSegment(sketch, "E12.52.3", {"start": v(10.9, 10.33) * mm, "end": v(11.44, 10.46) * mm});
            skArc(sketch, "E12.52.4", {"start": v(11.4, 9.73) * mm, "mid": v(11.4, 9.74) * mm, "end": v(11.41, 9.75) * mm});
            skLineSegment(sketch, "E12.52.5", {"start": v(11.41, 9.75) * mm, "end": v(11.6, 10.28) * mm});
            skArc(sketch, "E12.52.6", {"start": v(11.44, 10.46) * mm, "mid": v(11.52, 10.37) * mm, "end": v(11.6, 10.28) * mm});
            skLineSegment(sketch, "E12.53.0", {"start": v(9.98, 10.52) * mm, "end": v(10.33, 10.88) * mm});
            skLineSegment(sketch, "E12.53.1", {"start": v(9.42, 11.03) * mm, "end": v(9.74, 11.4) * mm});
            skArc(sketch, "E12.53.2", {"start": v(9.75, 11.41) * mm, "mid": v(9.74, 11.4) * mm, "end": v(9.73, 11.4) * mm});
            skLineSegment(sketch, "E12.53.3", {"start": v(9.75, 11.41) * mm, "end": v(10.28, 11.6) * mm});
            skArc(sketch, "E12.53.4", {"start": v(10.32, 10.87) * mm, "mid": v(10.32, 10.88) * mm, "end": v(10.33, 10.9) * mm});
            skLineSegment(sketch, "E12.53.5", {"start": v(10.33, 10.9) * mm, "end": v(10.46, 11.44) * mm});
            skArc(sketch, "E12.53.6", {"start": v(10.28, 11.6) * mm, "mid": v(10.37, 11.52) * mm, "end": v(10.46, 11.44) * mm});
            skLineSegment(sketch, "E12.54.0", {"start": v(8.83, 11.5) * mm, "end": v(9.13, 11.9) * mm});
            skLineSegment(sketch, "E12.54.1", {"start": v(8.21, 11.95) * mm, "end": v(8.5, 12.36) * mm});
            skArc(sketch, "E12.54.2", {"start": v(8.5, 12.37) * mm, "mid": v(8.5, 12.36) * mm, "end": v(8.49, 12.35) * mm});
            skLineSegment(sketch, "E12.54.3", {"start": v(8.5, 12.37) * mm, "end": v(9.01, 12.6) * mm});
            skArc(sketch, "E12.54.4", {"start": v(9.12, 11.89) * mm, "mid": v(9.13, 11.9) * mm, "end": v(9.13, 11.91) * mm});
            skLineSegment(sketch, "E12.54.5", {"start": v(9.13, 11.91) * mm, "end": v(9.2, 12.47) * mm});
            skArc(sketch, "E12.54.6", {"start": v(9.01, 12.6) * mm, "mid": v(9.11, 12.54) * mm, "end": v(9.2, 12.47) * mm});
            skLineSegment(sketch, "E12.55.0", {"start": v(7.58, 12.36) * mm, "end": v(7.84, 12.79) * mm});
            skLineSegment(sketch, "E12.55.1", {"start": v(6.92, 12.74) * mm, "end": v(7.16, 13.18) * mm});
            skArc(sketch, "E12.55.2", {"start": v(7.17, 13.19) * mm, "mid": v(7.16, 13.18) * mm, "end": v(7.15, 13.17) * mm});
            skLineSegment(sketch, "E12.55.3", {"start": v(7.17, 13.19) * mm, "end": v(7.65, 13.48) * mm});
            skArc(sketch, "E12.55.4", {"start": v(7.83, 12.78) * mm, "mid": v(7.84, 12.8) * mm, "end": v(7.84, 12.8) * mm});
            skLineSegment(sketch, "E12.55.5", {"start": v(7.84, 12.8) * mm, "end": v(7.85, 13.36) * mm});
            skArc(sketch, "E12.55.6", {"start": v(7.65, 13.48) * mm, "mid": v(7.75, 13.42) * mm, "end": v(7.85, 13.36) * mm});
            skLineSegment(sketch, "E12.56.0", {"start": v(6.24, 13.09) * mm, "end": v(6.46, 13.54) * mm});
            skLineSegment(sketch, "E12.56.1", {"start": v(5.55, 13.4) * mm, "end": v(5.74, 13.86) * mm});
            skArc(sketch, "E12.56.2", {"start": v(5.75, 13.87) * mm, "mid": v(5.74, 13.86) * mm, "end": v(5.74, 13.85) * mm});
            skLineSegment(sketch, "E12.56.3", {"start": v(5.75, 13.87) * mm, "end": v(6.2, 14.2) * mm});
            skArc(sketch, "E12.56.4", {"start": v(6.45, 13.53) * mm, "mid": v(6.46, 13.54) * mm, "end": v(6.46, 13.55) * mm});
            skLineSegment(sketch, "E12.56.5", {"start": v(6.46, 13.55) * mm, "end": v(6.41, 14.11) * mm});
            skArc(sketch, "E12.56.6", {"start": v(6.2, 14.2) * mm, "mid": v(6.3, 14.16) * mm, "end": v(6.41, 14.11) * mm});
            skLineSegment(sketch, "E12.57.0", {"start": v(4.84, 13.67) * mm, "end": v(5, 14.14) * mm});
            skLineSegment(sketch, "E12.57.1", {"start": v(4.12, 13.9) * mm, "end": v(4.26, 14.38) * mm});
            skArc(sketch, "E12.57.2", {"start": v(4.27, 14.4) * mm, "mid": v(4.26, 14.38) * mm, "end": v(4.26, 14.37) * mm});
            skLineSegment(sketch, "E12.57.3", {"start": v(4.27, 14.4) * mm, "end": v(4.68, 14.78) * mm});
            skArc(sketch, "E12.57.4", {"start": v(5, 14.13) * mm, "mid": v(5, 14.14) * mm, "end": v(5, 14.15) * mm});
            skLineSegment(sketch, "E12.57.5", {"start": v(5, 14.15) * mm, "end": v(4.9, 14.7) * mm});
            skArc(sketch, "E12.57.6", {"start": v(4.68, 14.78) * mm, "mid": v(4.79, 14.74) * mm, "end": v(4.9, 14.7) * mm});
            skLineSegment(sketch, "E12.58.0", {"start": v(3.38, 14.1) * mm, "end": v(3.5, 14.59) * mm});
            skLineSegment(sketch, "E12.58.1", {"start": v(2.64, 14.26) * mm, "end": v(2.73, 14.75) * mm});
            skArc(sketch, "E12.58.2", {"start": v(2.74, 14.76) * mm, "mid": v(2.74, 14.75) * mm, "end": v(2.73, 14.74) * mm});
            skLineSegment(sketch, "E12.58.3", {"start": v(2.74, 14.76) * mm, "end": v(3.1, 15.19) * mm});
            skArc(sketch, "E12.58.4", {"start": v(3.5, 14.57) * mm, "mid": v(3.5, 14.59) * mm, "end": v(3.5, 14.6) * mm});
            skLineSegment(sketch, "E12.58.5", {"start": v(3.5, 14.6) * mm, "end": v(3.34, 15.14) * mm});
            skArc(sketch, "E12.58.6", {"start": v(3.1, 15.19) * mm, "mid": v(3.22, 15.16) * mm, "end": v(3.34, 15.14) * mm});
            skLineSegment(sketch, "E12.59.0", {"start": v(1.9, 14.38) * mm, "end": v(1.96, 14.87) * mm});
            skLineSegment(sketch, "E12.59.1", {"start": v(1.14, 14.46) * mm, "end": v(1.18, 14.95) * mm});
            skArc(sketch, "E12.59.2", {"start": v(1.18, 14.96) * mm, "mid": v(1.18, 14.95) * mm, "end": v(1.18, 14.94) * mm});
            skLineSegment(sketch, "E12.59.3", {"start": v(1.18, 14.96) * mm, "end": v(1.5, 15.43) * mm});
            skArc(sketch, "E12.59.4", {"start": v(1.96, 14.86) * mm, "mid": v(1.96, 14.87) * mm, "end": v(1.95, 14.88) * mm});
            skLineSegment(sketch, "E12.59.5", {"start": v(1.95, 14.88) * mm, "end": v(1.74, 15.4) * mm});
            skArc(sketch, "E12.59.6", {"start": v(1.5, 15.43) * mm, "mid": v(1.62, 15.42) * mm, "end": v(1.74, 15.4) * mm});
            skSolve(sketch);
        }
        {
            var Q0;
            Q0 = qSketchRegion(id + "F0", true);
            extrude(context, id + "F1", {"entities" : qUnion([Q0]), "depth" : 10 * mm, "offsetDistance" : 25 * mm});
        }
        {
            var Q0;
            Q0=makeQuery(id+"F1.opExtrude","CAP_FACE",FACE,{"disambiguationData":[OSD([sQuery(id+"F0.wireOp",EDGE,"E0"),sQuery(id+"F0.wireOp",EDGE,"E5"),sQuery(id+"F0.wireOp",EDGE,"E6"),sQuery(id+"F0.wireOp",EDGE,"E7"),sQuery(id+"F0.wireOp",EDGE,"E8"),sQuery(id+"F0.wireOp",EDGE,"E9"),sQuery(id+"F0.wireOp",EDGE,"E10.filletArc"),sQuery(id+"F0.wireOp",EDGE,"E11.filletArc"),sQuery(id+"F0.wireOp",EDGE,"E12.1.0"),sQuery(id+"F0.wireOp",EDGE,"E12.1.1"),sQuery(id+"F0.wireOp",EDGE,"E12.1.2"),sQuery(id+"F0.wireOp",EDGE,"E12.1.3"),sQuery(id+"F0.wireOp",EDGE,"E12.1.4"),sQuery(id+"F0.wireOp",EDGE,"E12.1.5"),sQuery(id+"F0.wireOp",EDGE,"E12.1.6"),sQuery(id+"F0.wireOp",EDGE,"E12.2.0"),sQuery(id+"F0.wireOp",EDGE,"E12.2.1"),sQuery(id+"F0.wireOp",EDGE,"E12.2.2"),sQuery(id+"F0.wireOp",EDGE,"E12.2.3"),sQuery(id+"F0.wireOp",EDGE,"E12.2.4"),sQuery(id+"F0.wireOp",EDGE,"E12.2.5"),sQuery(id+"F0.wireOp",EDGE,"E12.2.6"),sQuery(id+"F0.wireOp",EDGE,"E12.3.0"),sQuery(id+"F0.wireOp",EDGE,"E12.3.1"),sQuery(id+"F0.wireOp",EDGE,"E12.3.2"),sQuery(id+"F0.wireOp",EDGE,"E12.3.3"),sQuery(id+"F0.wireOp",EDGE,"E12.3.4"),sQuery(id+"F0.wireOp",EDGE,"E12.3.5"),sQuery(id+"F0.wireOp",EDGE,"E12.3.6"),sQuery(id+"F0.wireOp",EDGE,"E12.4.0"),sQuery(id+"F0.wireOp",EDGE,"E12.4.1"),sQuery(id+"F0.wireOp",EDGE,"E12.4.2"),sQuery(id+"F0.wireOp",EDGE,"E12.4.3"),sQuery(id+"F0.wireOp",EDGE,"E12.4.4"),sQuery(id+"F0.wireOp",EDGE,"E12.4.5"),sQuery(id+"F0.wireOp",EDGE,"E12.4.6"),sQuery(id+"F0.wireOp",EDGE,"E12.5.0"),sQuery(id+"F0.wireOp",EDGE,"E12.5.1"),sQuery(id+"F0.wireOp",EDGE,"E12.5.2"),sQuery(id+"F0.wireOp",EDGE,"E12.5.3"),sQuery(id+"F0.wireOp",EDGE,"E12.5.4"),sQuery(id+"F0.wireOp",EDGE,"E12.5.5"),sQuery(id+"F0.wireOp",EDGE,"E12.5.6"),sQuery(id+"F0.wireOp",EDGE,"E12.6.0"),sQuery(id+"F0.wireOp",EDGE,"E12.6.1"),sQuery(id+"F0.wireOp",EDGE,"E12.6.2"),sQuery(id+"F0.wireOp",EDGE,"E12.6.3"),sQuery(id+"F0.wireOp",EDGE,"E12.6.4"),sQuery(id+"F0.wireOp",EDGE,"E12.6.5"),sQuery(id+"F0.wireOp",EDGE,"E12.6.6"),sQuery(id+"F0.wireOp",EDGE,"E12.7.0"),sQuery(id+"F0.wireOp",EDGE,"E12.7.1"),sQuery(id+"F0.wireOp",EDGE,"E12.7.2"),sQuery(id+"F0.wireOp",EDGE,"E12.7.3"),sQuery(id+"F0.wireOp",EDGE,"E12.7.4"),sQuery(id+"F0.wireOp",EDGE,"E12.7.5"),sQuery(id+"F0.wireOp",EDGE,"E12.7.6"),sQuery(id+"F0.wireOp",EDGE,"E12.8.0"),sQuery(id+"F0.wireOp",EDGE,"E12.8.1"),sQuery(id+"F0.wireOp",EDGE,"E12.8.2"),sQuery(id+"F0.wireOp",EDGE,"E12.8.3"),sQuery(id+"F0.wireOp",EDGE,"E12.8.4"),sQuery(id+"F0.wireOp",EDGE,"E12.8.5"),sQuery(id+"F0.wireOp",EDGE,"E12.8.6"),sQuery(id+"F0.wireOp",EDGE,"E12.9.0"),sQuery(id+"F0.wireOp",EDGE,"E12.9.1"),sQuery(id+"F0.wireOp",EDGE,"E12.9.2"),sQuery(id+"F0.wireOp",EDGE,"E12.9.3"),sQuery(id+"F0.wireOp",EDGE,"E12.9.4"),sQuery(id+"F0.wireOp",EDGE,"E12.9.5"),sQuery(id+"F0.wireOp",EDGE,"E12.9.6"),sQuery(id+"F0.wireOp",EDGE,"E12.10.0"),sQuery(id+"F0.wireOp",EDGE,"E12.10.1"),sQuery(id+"F0.wireOp",EDGE,"E12.10.2"),sQuery(id+"F0.wireOp",EDGE,"E12.10.3"),sQuery(id+"F0.wireOp",EDGE,"E12.10.4"),sQuery(id+"F0.wireOp",EDGE,"E12.10.5"),sQuery(id+"F0.wireOp",EDGE,"E12.10.6"),sQuery(id+"F0.wireOp",EDGE,"E12.11.0"),sQuery(id+"F0.wireOp",EDGE,"E12.11.1"),sQuery(id+"F0.wireOp",EDGE,"E12.11.2"),sQuery(id+"F0.wireOp",EDGE,"E12.11.3"),sQuery(id+"F0.wireOp",EDGE,"E12.11.4"),sQuery(id+"F0.wireOp",EDGE,"E12.11.5"),sQuery(id+"F0.wireOp",EDGE,"E12.11.6"),sQuery(id+"F0.wireOp",EDGE,"E12.12.0"),sQuery(id+"F0.wireOp",EDGE,"E12.12.1"),sQuery(id+"F0.wireOp",EDGE,"E12.12.2"),sQuery(id+"F0.wireOp",EDGE,"E12.12.3"),sQuery(id+"F0.wireOp",EDGE,"E12.12.4"),sQuery(id+"F0.wireOp",EDGE,"E12.12.5"),sQuery(id+"F0.wireOp",EDGE,"E12.12.6"),sQuery(id+"F0.wireOp",EDGE,"E12.13.0"),sQuery(id+"F0.wireOp",EDGE,"E12.13.1"),sQuery(id+"F0.wireOp",EDGE,"E12.13.2"),sQuery(id+"F0.wireOp",EDGE,"E12.13.3"),sQuery(id+"F0.wireOp",EDGE,"E12.13.4"),sQuery(id+"F0.wireOp",EDGE,"E12.13.5"),sQuery(id+"F0.wireOp",EDGE,"E12.13.6"),sQuery(id+"F0.wireOp",EDGE,"E12.14.0"),sQuery(id+"F0.wireOp",EDGE,"E12.14.1"),sQuery(id+"F0.wireOp",EDGE,"E12.14.2"),sQuery(id+"F0.wireOp",EDGE,"E12.14.3"),sQuery(id+"F0.wireOp",EDGE,"E12.14.4"),sQuery(id+"F0.wireOp",EDGE,"E12.14.5"),sQuery(id+"F0.wireOp",EDGE,"E12.14.6"),sQuery(id+"F0.wireOp",EDGE,"E12.15.0"),sQuery(id+"F0.wireOp",EDGE,"E12.15.1"),sQuery(id+"F0.wireOp",EDGE,"E12.15.2"),sQuery(id+"F0.wireOp",EDGE,"E12.15.3"),sQuery(id+"F0.wireOp",EDGE,"E12.15.4"),sQuery(id+"F0.wireOp",EDGE,"E12.15.5"),sQuery(id+"F0.wireOp",EDGE,"E12.15.6"),sQuery(id+"F0.wireOp",EDGE,"E12.16.0"),sQuery(id+"F0.wireOp",EDGE,"E12.16.1"),sQuery(id+"F0.wireOp",EDGE,"E12.16.2"),sQuery(id+"F0.wireOp",EDGE,"E12.16.3"),sQuery(id+"F0.wireOp",EDGE,"E12.16.4"),sQuery(id+"F0.wireOp",EDGE,"E12.16.5"),sQuery(id+"F0.wireOp",EDGE,"E12.16.6"),sQuery(id+"F0.wireOp",EDGE,"E12.17.0"),sQuery(id+"F0.wireOp",EDGE,"E12.17.1"),sQuery(id+"F0.wireOp",EDGE,"E12.17.2"),sQuery(id+"F0.wireOp",EDGE,"E12.17.3"),sQuery(id+"F0.wireOp",EDGE,"E12.17.4"),sQuery(id+"F0.wireOp",EDGE,"E12.17.5"),sQuery(id+"F0.wireOp",EDGE,"E12.17.6"),sQuery(id+"F0.wireOp",EDGE,"E12.18.0"),sQuery(id+"F0.wireOp",EDGE,"E12.18.1"),sQuery(id+"F0.wireOp",EDGE,"E12.18.2"),sQuery(id+"F0.wireOp",EDGE,"E12.18.3"),sQuery(id+"F0.wireOp",EDGE,"E12.18.4"),sQuery(id+"F0.wireOp",EDGE,"E12.18.5"),sQuery(id+"F0.wireOp",EDGE,"E12.18.6"),sQuery(id+"F0.wireOp",EDGE,"E12.19.0"),sQuery(id+"F0.wireOp",EDGE,"E12.19.1"),sQuery(id+"F0.wireOp",EDGE,"E12.19.2"),sQuery(id+"F0.wireOp",EDGE,"E12.19.3"),sQuery(id+"F0.wireOp",EDGE,"E12.19.4"),sQuery(id+"F0.wireOp",EDGE,"E12.19.5"),sQuery(id+"F0.wireOp",EDGE,"E12.19.6"),sQuery(id+"F0.wireOp",EDGE,"E12.20.0"),sQuery(id+"F0.wireOp",EDGE,"E12.20.1"),sQuery(id+"F0.wireOp",EDGE,"E12.20.2"),sQuery(id+"F0.wireOp",EDGE,"E12.20.3"),sQuery(id+"F0.wireOp",EDGE,"E12.20.4"),sQuery(id+"F0.wireOp",EDGE,"E12.20.5"),sQuery(id+"F0.wireOp",EDGE,"E12.20.6"),sQuery(id+"F0.wireOp",EDGE,"E12.21.0"),sQuery(id+"F0.wireOp",EDGE,"E12.21.1"),sQuery(id+"F0.wireOp",EDGE,"E12.21.2"),sQuery(id+"F0.wireOp",EDGE,"E12.21.3"),sQuery(id+"F0.wireOp",EDGE,"E12.21.4"),sQuery(id+"F0.wireOp",EDGE,"E12.21.5"),sQuery(id+"F0.wireOp",EDGE,"E12.21.6"),sQuery(id+"F0.wireOp",EDGE,"E12.22.0"),sQuery(id+"F0.wireOp",EDGE,"E12.22.1"),sQuery(id+"F0.wireOp",EDGE,"E12.22.2"),sQuery(id+"F0.wireOp",EDGE,"E12.22.3"),sQuery(id+"F0.wireOp",EDGE,"E12.22.4"),sQuery(id+"F0.wireOp",EDGE,"E12.22.5"),sQuery(id+"F0.wireOp",EDGE,"E12.22.6"),sQuery(id+"F0.wireOp",EDGE,"E12.23.0"),sQuery(id+"F0.wireOp",EDGE,"E12.23.1"),sQuery(id+"F0.wireOp",EDGE,"E12.23.2"),sQuery(id+"F0.wireOp",EDGE,"E12.23.3"),sQuery(id+"F0.wireOp",EDGE,"E12.23.4"),sQuery(id+"F0.wireOp",EDGE,"E12.23.5"),sQuery(id+"F0.wireOp",EDGE,"E12.23.6"),sQuery(id+"F0.wireOp",EDGE,"E12.24.0"),sQuery(id+"F0.wireOp",EDGE,"E12.24.1"),sQuery(id+"F0.wireOp",EDGE,"E12.24.2"),sQuery(id+"F0.wireOp",EDGE,"E12.24.3"),sQuery(id+"F0.wireOp",EDGE,"E12.24.4"),sQuery(id+"F0.wireOp",EDGE,"E12.24.5"),sQuery(id+"F0.wireOp",EDGE,"E12.24.6"),sQuery(id+"F0.wireOp",EDGE,"E12.25.0"),sQuery(id+"F0.wireOp",EDGE,"E12.25.1"),sQuery(id+"F0.wireOp",EDGE,"E12.25.2"),sQuery(id+"F0.wireOp",EDGE,"E12.25.3"),sQuery(id+"F0.wireOp",EDGE,"E12.25.4"),sQuery(id+"F0.wireOp",EDGE,"E12.25.5"),sQuery(id+"F0.wireOp",EDGE,"E12.25.6"),sQuery(id+"F0.wireOp",EDGE,"E12.26.0"),sQuery(id+"F0.wireOp",EDGE,"E12.26.1"),sQuery(id+"F0.wireOp",EDGE,"E12.26.2"),sQuery(id+"F0.wireOp",EDGE,"E12.26.3"),sQuery(id+"F0.wireOp",EDGE,"E12.26.4"),sQuery(id+"F0.wireOp",EDGE,"E12.26.5"),sQuery(id+"F0.wireOp",EDGE,"E12.26.6"),sQuery(id+"F0.wireOp",EDGE,"E12.27.0"),sQuery(id+"F0.wireOp",EDGE,"E12.27.1"),sQuery(id+"F0.wireOp",EDGE,"E12.27.2"),sQuery(id+"F0.wireOp",EDGE,"E12.27.3"),sQuery(id+"F0.wireOp",EDGE,"E12.27.4"),sQuery(id+"F0.wireOp",EDGE,"E12.27.5"),sQuery(id+"F0.wireOp",EDGE,"E12.27.6"),sQuery(id+"F0.wireOp",EDGE,"E12.28.0"),sQuery(id+"F0.wireOp",EDGE,"E12.28.1"),sQuery(id+"F0.wireOp",EDGE,"E12.28.2"),sQuery(id+"F0.wireOp",EDGE,"E12.28.3"),sQuery(id+"F0.wireOp",EDGE,"E12.28.4"),sQuery(id+"F0.wireOp",EDGE,"E12.28.5"),sQuery(id+"F0.wireOp",EDGE,"E12.28.6"),sQuery(id+"F0.wireOp",EDGE,"E12.29.0"),sQuery(id+"F0.wireOp",EDGE,"E12.29.1"),sQuery(id+"F0.wireOp",EDGE,"E12.29.2"),sQuery(id+"F0.wireOp",EDGE,"E12.29.3"),sQuery(id+"F0.wireOp",EDGE,"E12.29.4"),sQuery(id+"F0.wireOp",EDGE,"E12.29.5"),sQuery(id+"F0.wireOp",EDGE,"E12.29.6"),sQuery(id+"F0.wireOp",EDGE,"E12.30.0"),sQuery(id+"F0.wireOp",EDGE,"E12.30.1"),sQuery(id+"F0.wireOp",EDGE,"E12.30.2"),sQuery(id+"F0.wireOp",EDGE,"E12.30.3"),sQuery(id+"F0.wireOp",EDGE,"E12.30.4"),sQuery(id+"F0.wireOp",EDGE,"E12.30.5"),sQuery(id+"F0.wireOp",EDGE,"E12.30.6"),sQuery(id+"F0.wireOp",EDGE,"E12.31.0"),sQuery(id+"F0.wireOp",EDGE,"E12.31.1"),sQuery(id+"F0.wireOp",EDGE,"E12.31.2"),sQuery(id+"F0.wireOp",EDGE,"E12.31.3"),sQuery(id+"F0.wireOp",EDGE,"E12.31.4"),sQuery(id+"F0.wireOp",EDGE,"E12.31.5"),sQuery(id+"F0.wireOp",EDGE,"E12.31.6"),sQuery(id+"F0.wireOp",EDGE,"E12.32.0"),sQuery(id+"F0.wireOp",EDGE,"E12.32.1"),sQuery(id+"F0.wireOp",EDGE,"E12.32.2"),sQuery(id+"F0.wireOp",EDGE,"E12.32.3"),sQuery(id+"F0.wireOp",EDGE,"E12.32.4"),sQuery(id+"F0.wireOp",EDGE,"E12.32.5"),sQuery(id+"F0.wireOp",EDGE,"E12.32.6"),sQuery(id+"F0.wireOp",EDGE,"E12.33.0"),sQuery(id+"F0.wireOp",EDGE,"E12.33.1"),sQuery(id+"F0.wireOp",EDGE,"E12.33.2"),sQuery(id+"F0.wireOp",EDGE,"E12.33.3"),sQuery(id+"F0.wireOp",EDGE,"E12.33.4"),sQuery(id+"F0.wireOp",EDGE,"E12.33.5"),sQuery(id+"F0.wireOp",EDGE,"E12.33.6"),sQuery(id+"F0.wireOp",EDGE,"E12.34.0"),sQuery(id+"F0.wireOp",EDGE,"E12.34.1"),sQuery(id+"F0.wireOp",EDGE,"E12.34.2"),sQuery(id+"F0.wireOp",EDGE,"E12.34.3"),sQuery(id+"F0.wireOp",EDGE,"E12.34.4"),sQuery(id+"F0.wireOp",EDGE,"E12.34.5"),sQuery(id+"F0.wireOp",EDGE,"E12.34.6"),sQuery(id+"F0.wireOp",EDGE,"E12.35.0"),sQuery(id+"F0.wireOp",EDGE,"E12.35.1"),sQuery(id+"F0.wireOp",EDGE,"E12.35.2"),sQuery(id+"F0.wireOp",EDGE,"E12.35.3"),sQuery(id+"F0.wireOp",EDGE,"E12.35.4"),sQuery(id+"F0.wireOp",EDGE,"E12.35.5"),sQuery(id+"F0.wireOp",EDGE,"E12.35.6"),sQuery(id+"F0.wireOp",EDGE,"E12.36.0"),sQuery(id+"F0.wireOp",EDGE,"E12.36.1"),sQuery(id+"F0.wireOp",EDGE,"E12.36.2"),sQuery(id+"F0.wireOp",EDGE,"E12.36.3"),sQuery(id+"F0.wireOp",EDGE,"E12.36.4"),sQuery(id+"F0.wireOp",EDGE,"E12.36.5"),sQuery(id+"F0.wireOp",EDGE,"E12.36.6"),sQuery(id+"F0.wireOp",EDGE,"E12.37.0"),sQuery(id+"F0.wireOp",EDGE,"E12.37.1"),sQuery(id+"F0.wireOp",EDGE,"E12.37.2"),sQuery(id+"F0.wireOp",EDGE,"E12.37.3"),sQuery(id+"F0.wireOp",EDGE,"E12.37.4"),sQuery(id+"F0.wireOp",EDGE,"E12.37.5"),sQuery(id+"F0.wireOp",EDGE,"E12.37.6"),sQuery(id+"F0.wireOp",EDGE,"E12.38.0"),sQuery(id+"F0.wireOp",EDGE,"E12.38.1"),sQuery(id+"F0.wireOp",EDGE,"E12.38.2"),sQuery(id+"F0.wireOp",EDGE,"E12.38.3"),sQuery(id+"F0.wireOp",EDGE,"E12.38.4"),sQuery(id+"F0.wireOp",EDGE,"E12.38.5"),sQuery(id+"F0.wireOp",EDGE,"E12.38.6"),sQuery(id+"F0.wireOp",EDGE,"E12.39.0"),sQuery(id+"F0.wireOp",EDGE,"E12.39.1"),sQuery(id+"F0.wireOp",EDGE,"E12.39.2"),sQuery(id+"F0.wireOp",EDGE,"E12.39.3"),sQuery(id+"F0.wireOp",EDGE,"E12.39.4"),sQuery(id+"F0.wireOp",EDGE,"E12.39.5"),sQuery(id+"F0.wireOp",EDGE,"E12.39.6"),sQuery(id+"F0.wireOp",EDGE,"E12.40.0"),sQuery(id+"F0.wireOp",EDGE,"E12.40.1"),sQuery(id+"F0.wireOp",EDGE,"E12.40.2"),sQuery(id+"F0.wireOp",EDGE,"E12.40.3"),sQuery(id+"F0.wireOp",EDGE,"E12.40.4"),sQuery(id+"F0.wireOp",EDGE,"E12.40.5"),sQuery(id+"F0.wireOp",EDGE,"E12.40.6"),sQuery(id+"F0.wireOp",EDGE,"E12.41.0"),sQuery(id+"F0.wireOp",EDGE,"E12.41.1"),sQuery(id+"F0.wireOp",EDGE,"E12.41.2"),sQuery(id+"F0.wireOp",EDGE,"E12.41.3"),sQuery(id+"F0.wireOp",EDGE,"E12.41.4"),sQuery(id+"F0.wireOp",EDGE,"E12.41.5"),sQuery(id+"F0.wireOp",EDGE,"E12.41.6"),sQuery(id+"F0.wireOp",EDGE,"E12.42.0"),sQuery(id+"F0.wireOp",EDGE,"E12.42.1"),sQuery(id+"F0.wireOp",EDGE,"E12.42.2"),sQuery(id+"F0.wireOp",EDGE,"E12.42.3"),sQuery(id+"F0.wireOp",EDGE,"E12.42.4"),sQuery(id+"F0.wireOp",EDGE,"E12.42.5"),sQuery(id+"F0.wireOp",EDGE,"E12.42.6"),sQuery(id+"F0.wireOp",EDGE,"E12.43.0"),sQuery(id+"F0.wireOp",EDGE,"E12.43.1"),sQuery(id+"F0.wireOp",EDGE,"E12.43.2"),sQuery(id+"F0.wireOp",EDGE,"E12.43.3"),sQuery(id+"F0.wireOp",EDGE,"E12.43.4"),sQuery(id+"F0.wireOp",EDGE,"E12.43.5"),sQuery(id+"F0.wireOp",EDGE,"E12.43.6"),sQuery(id+"F0.wireOp",EDGE,"E12.44.0"),sQuery(id+"F0.wireOp",EDGE,"E12.44.1"),sQuery(id+"F0.wireOp",EDGE,"E12.44.2"),sQuery(id+"F0.wireOp",EDGE,"E12.44.3"),sQuery(id+"F0.wireOp",EDGE,"E12.44.4"),sQuery(id+"F0.wireOp",EDGE,"E12.44.5"),sQuery(id+"F0.wireOp",EDGE,"E12.44.6"),sQuery(id+"F0.wireOp",EDGE,"E12.45.0"),sQuery(id+"F0.wireOp",EDGE,"E12.45.1"),sQuery(id+"F0.wireOp",EDGE,"E12.45.2"),sQuery(id+"F0.wireOp",EDGE,"E12.45.3"),sQuery(id+"F0.wireOp",EDGE,"E12.45.4"),sQuery(id+"F0.wireOp",EDGE,"E12.45.5"),sQuery(id+"F0.wireOp",EDGE,"E12.45.6"),sQuery(id+"F0.wireOp",EDGE,"E12.46.0"),sQuery(id+"F0.wireOp",EDGE,"E12.46.1"),sQuery(id+"F0.wireOp",EDGE,"E12.46.2"),sQuery(id+"F0.wireOp",EDGE,"E12.46.3"),sQuery(id+"F0.wireOp",EDGE,"E12.46.4"),sQuery(id+"F0.wireOp",EDGE,"E12.46.5"),sQuery(id+"F0.wireOp",EDGE,"E12.46.6"),sQuery(id+"F0.wireOp",EDGE,"E12.47.0"),sQuery(id+"F0.wireOp",EDGE,"E12.47.1"),sQuery(id+"F0.wireOp",EDGE,"E12.47.2"),sQuery(id+"F0.wireOp",EDGE,"E12.47.3"),sQuery(id+"F0.wireOp",EDGE,"E12.47.4"),sQuery(id+"F0.wireOp",EDGE,"E12.47.5"),sQuery(id+"F0.wireOp",EDGE,"E12.47.6"),sQuery(id+"F0.wireOp",EDGE,"E12.48.0"),sQuery(id+"F0.wireOp",EDGE,"E12.48.1"),sQuery(id+"F0.wireOp",EDGE,"E12.48.2"),sQuery(id+"F0.wireOp",EDGE,"E12.48.3"),sQuery(id+"F0.wireOp",EDGE,"E12.48.4"),sQuery(id+"F0.wireOp",EDGE,"E12.48.5"),sQuery(id+"F0.wireOp",EDGE,"E12.48.6"),sQuery(id+"F0.wireOp",EDGE,"E12.49.0"),sQuery(id+"F0.wireOp",EDGE,"E12.49.1"),sQuery(id+"F0.wireOp",EDGE,"E12.49.2"),sQuery(id+"F0.wireOp",EDGE,"E12.49.3"),sQuery(id+"F0.wireOp",EDGE,"E12.49.4"),sQuery(id+"F0.wireOp",EDGE,"E12.49.5"),sQuery(id+"F0.wireOp",EDGE,"E12.49.6"),sQuery(id+"F0.wireOp",EDGE,"E12.50.0"),sQuery(id+"F0.wireOp",EDGE,"E12.50.1"),sQuery(id+"F0.wireOp",EDGE,"E12.50.2"),sQuery(id+"F0.wireOp",EDGE,"E12.50.3"),sQuery(id+"F0.wireOp",EDGE,"E12.50.4"),sQuery(id+"F0.wireOp",EDGE,"E12.50.5"),sQuery(id+"F0.wireOp",EDGE,"E12.50.6"),sQuery(id+"F0.wireOp",EDGE,"E12.51.0"),sQuery(id+"F0.wireOp",EDGE,"E12.51.1"),sQuery(id+"F0.wireOp",EDGE,"E12.51.2"),sQuery(id+"F0.wireOp",EDGE,"E12.51.3"),sQuery(id+"F0.wireOp",EDGE,"E12.51.4"),sQuery(id+"F0.wireOp",EDGE,"E12.51.5"),sQuery(id+"F0.wireOp",EDGE,"E12.51.6"),sQuery(id+"F0.wireOp",EDGE,"E12.52.0"),sQuery(id+"F0.wireOp",EDGE,"E12.52.1"),sQuery(id+"F0.wireOp",EDGE,"E12.52.2"),sQuery(id+"F0.wireOp",EDGE,"E12.52.3"),sQuery(id+"F0.wireOp",EDGE,"E12.52.4"),sQuery(id+"F0.wireOp",EDGE,"E12.52.5"),sQuery(id+"F0.wireOp",EDGE,"E12.52.6"),sQuery(id+"F0.wireOp",EDGE,"E12.53.0"),sQuery(id+"F0.wireOp",EDGE,"E12.53.1"),sQuery(id+"F0.wireOp",EDGE,"E12.53.2"),sQuery(id+"F0.wireOp",EDGE,"E12.53.3"),sQuery(id+"F0.wireOp",EDGE,"E12.53.4"),sQuery(id+"F0.wireOp",EDGE,"E12.53.5"),sQuery(id+"F0.wireOp",EDGE,"E12.53.6"),sQuery(id+"F0.wireOp",EDGE,"E12.54.0"),sQuery(id+"F0.wireOp",EDGE,"E12.54.1"),sQuery(id+"F0.wireOp",EDGE,"E12.54.2"),sQuery(id+"F0.wireOp",EDGE,"E12.54.3"),sQuery(id+"F0.wireOp",EDGE,"E12.54.4"),sQuery(id+"F0.wireOp",EDGE,"E12.54.5"),sQuery(id+"F0.wireOp",EDGE,"E12.54.6"),sQuery(id+"F0.wireOp",EDGE,"E12.55.0"),sQuery(id+"F0.wireOp",EDGE,"E12.55.1"),sQuery(id+"F0.wireOp",EDGE,"E12.55.2"),sQuery(id+"F0.wireOp",EDGE,"E12.55.3"),sQuery(id+"F0.wireOp",EDGE,"E12.55.4"),sQuery(id+"F0.wireOp",EDGE,"E12.55.5"),sQuery(id+"F0.wireOp",EDGE,"E12.55.6"),sQuery(id+"F0.wireOp",EDGE,"E12.56.0"),sQuery(id+"F0.wireOp",EDGE,"E12.56.1"),sQuery(id+"F0.wireOp",EDGE,"E12.56.2"),sQuery(id+"F0.wireOp",EDGE,"E12.56.3"),sQuery(id+"F0.wireOp",EDGE,"E12.56.4"),sQuery(id+"F0.wireOp",EDGE,"E12.56.5"),sQuery(id+"F0.wireOp",EDGE,"E12.56.6"),sQuery(id+"F0.wireOp",EDGE,"E12.57.0"),sQuery(id+"F0.wireOp",EDGE,"E12.57.1"),sQuery(id+"F0.wireOp",EDGE,"E12.57.2"),sQuery(id+"F0.wireOp",EDGE,"E12.57.3"),sQuery(id+"F0.wireOp",EDGE,"E12.57.4"),sQuery(id+"F0.wireOp",EDGE,"E12.57.5"),sQuery(id+"F0.wireOp",EDGE,"E12.57.6"),sQuery(id+"F0.wireOp",EDGE,"E12.58.0"),sQuery(id+"F0.wireOp",EDGE,"E12.58.1"),sQuery(id+"F0.wireOp",EDGE,"E12.58.2"),sQuery(id+"F0.wireOp",EDGE,"E12.58.3"),sQuery(id+"F0.wireOp",EDGE,"E12.58.4"),sQuery(id+"F0.wireOp",EDGE,"E12.58.5"),sQuery(id+"F0.wireOp",EDGE,"E12.58.6"),sQuery(id+"F0.wireOp",EDGE,"E12.59.0"),sQuery(id+"F0.wireOp",EDGE,"E12.59.1"),sQuery(id+"F0.wireOp",EDGE,"E12.59.2"),sQuery(id+"F0.wireOp",EDGE,"E12.59.3"),sQuery(id+"F0.wireOp",EDGE,"E12.59.4"),sQuery(id+"F0.wireOp",EDGE,"E12.59.5"),sQuery(id+"F0.wireOp",EDGE,"E12.59.6")])],"isStart":true});
            var sketch = newSketch(context, id + "F2", { "sketchPlane" : qUnion([Q0])});
            skCircle(sketch, "E13", {"center": v(0, 0) * mm, "radius": 2.25 * mm});
            skSolve(sketch);
        }
        {
            var Q0;
            Q0 = qSketchRegion(id + "F2", true);
            extrude(context, id + "F3", {"entities" : qUnion([Q0]), "operationType" : NewBodyOperationType.REMOVE, "endBound" : BoundingType.THROUGH_ALL, "oppositeDirection" : true, "depth" : 25 * mm, "offsetDistance" : 25 * mm});
        }
    });
